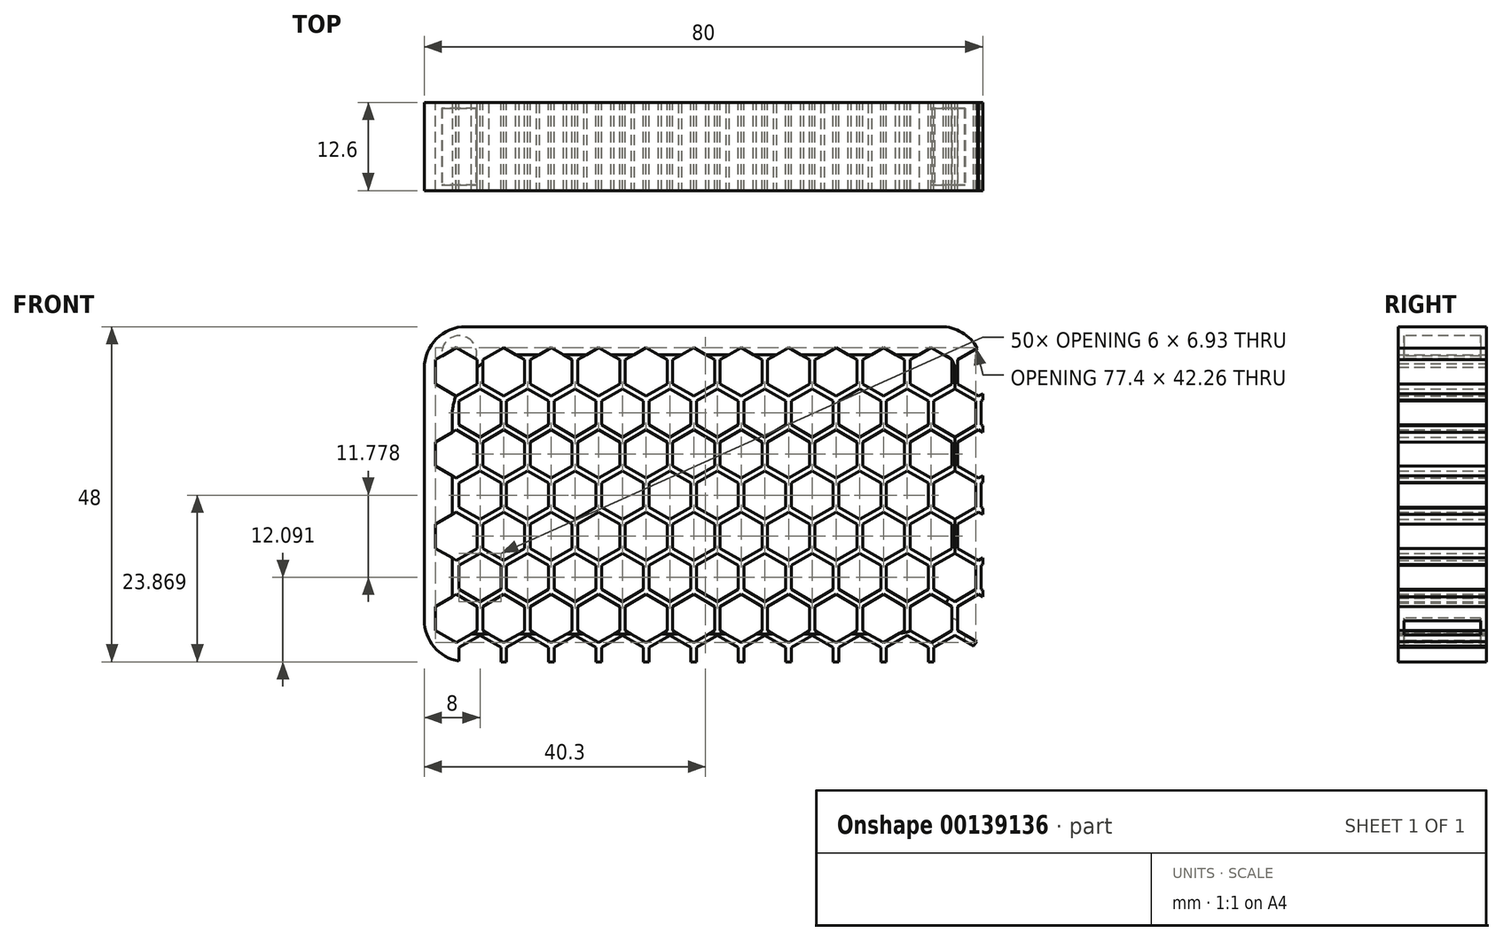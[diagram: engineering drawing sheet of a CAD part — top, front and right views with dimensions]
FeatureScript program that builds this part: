
annotation { "Feature Type Name" : "Feature", "Feature Type Description" : "" }
export const myFeature = defineFeature(function(context is Context, id is Id, definition is map)
    precondition{}
    {
        {
            var Q0;
            Q0=qCreatedBy(makeId("Front.planeOp"),FACE);
            var sketch = newSketch(context, id + "F0", { "sketchPlane" : qUnion([Q0])});
            skLineSegment(sketch, "E0.bottom", {"start": v(-34, 24) * mm, "end": v(34, 24) * mm});
            skLineSegment(sketch, "E0.top", {"start": v(-34, -24) * mm, "end": v(34, -24) * mm});
            skLineSegment(sketch, "E0.left", {"start": v(-40, 18) * mm, "end": v(-40, -18) * mm});
            skLineSegment(sketch, "E0.right", {"start": v(40, 18) * mm, "end": v(40, -18) * mm});
            skPoint(sketch, "E1", {"position": v(0, 24) * mm});
            skPoint(sketch, "E2", {"position": v(-40, 0) * mm});
            skPoint(sketch, "E3.visualSharp", {"position": v(-40, 24) * mm});
            skArc(sketch, "E3.filletArc", {"start": v(-34, 24) * mm, "mid": v(-38.24, 22.24) * mm, "end": v(-40, 18) * mm});
            skPoint(sketch, "E4.visualSharp", {"position": v(40, 24) * mm});
            skArc(sketch, "E4.filletArc", {"start": v(40, 18) * mm, "mid": v(38.24, 22.24) * mm, "end": v(34, 24) * mm});
            skPoint(sketch, "E5.visualSharp", {"position": v(40, -24) * mm});
            skArc(sketch, "E5.filletArc", {"start": v(34, -24) * mm, "mid": v(38.24, -22.24) * mm, "end": v(40, -18) * mm});
            skPoint(sketch, "E6.visualSharp", {"position": v(-40, -24) * mm});
            skArc(sketch, "E6.filletArc", {"start": v(-40, -18) * mm, "mid": v(-38.24, -22.24) * mm, "end": v(-34, -24) * mm});
            skLineSegment(sketch, "E7.0", {"start": v(-27, 20) * mm, "end": v(34, 20) * mm});
            skLineSegment(sketch, "E7.1", {"start": v(-36, 11) * mm, "end": v(-36, -18) * mm});
            skLineSegment(sketch, "E7.2", {"start": v(-34, -20) * mm, "end": v(27, -20) * mm});
            skLineSegment(sketch, "E7.3", {"start": v(36, 18) * mm, "end": v(36, -11) * mm});
            skPoint(sketch, "E8.visualSharp", {"position": v(36, 20) * mm});
            skArc(sketch, "E8.filletArc", {"start": v(36, 18) * mm, "mid": v(35.41, 19.41) * mm, "end": v(34, 20) * mm});
            skPoint(sketch, "E9.visualSharp", {"position": v(36, -20) * mm});
            skPoint(sketch, "E10.visualSharp", {"position": v(-36, -20) * mm});
            skArc(sketch, "E10.filletArc", {"start": v(-36, -18) * mm, "mid": v(-35.41, -19.41) * mm, "end": v(-34, -20) * mm});
            skPoint(sketch, "E11.visualSharp", {"position": v(-36, 20) * mm});
            skArc(sketch, "E12.filletArc", {"start": v(-27, 20) * mm, "mid": v(-33.36, 17.36) * mm, "end": v(-36, 11) * mm});
            skArc(sketch, "E13.filletArc", {"start": v(27, -20) * mm, "mid": v(33.36, -17.36) * mm, "end": v(36, -11) * mm});
            skSolve(sketch);
        }
        {
            var Q0;
            Q0=makeQuery(id+"F0.imprint","IMPRINT",FACE,{"disambiguationData":[TD([[makeQuery(id+"F0.imprint","IMPRINT",EDGE,{"derivedFrom":sQuery(id+"F0.wireOp",EDGE,"E0.bottom")}),-1.0]])]});
            var Q1;
            {var subQ0=sQuery(id+"F0.wireOp",EDGE,"E11.filletArc");Q1=makeQuery(id+"F0.imprint","IMPRINT",FACE,{"disambiguationData":[TD([[makeQuery(id+"F0.imprint","IMPRINT",EDGE,{"derivedFrom":subQ0}),1.0]])]});}
            var Q2;
            {var subQ0=sQuery(id+"F0.wireOp",EDGE,"E11.filletArc");Q2=makeQuery(id+"F0.imprint","IMPRINT",FACE,{"disambiguationData":[TD([[makeQuery(id+"F0.imprint","IMPRINT",EDGE,{"derivedFrom":subQ0}),-1.0]])]});}
            extrude(context, id + "F1", {"entities" : qUnion([Q0, Q1, Q2]), "endBound" : BoundingType.SYMMETRIC, "depth" : 12.6 * mm});
        }
        {
            var Q0;
            Q0=makeQuery(id+"F1.opExtrude","CAP_FACE",FACE,{"disambiguationData":[OSD([sQuery(id+"F0.wireOp",EDGE,"E0.bottom"),sQuery(id+"F0.wireOp",EDGE,"E0.top"),sQuery(id+"F0.wireOp",EDGE,"E0.left"),sQuery(id+"F0.wireOp",EDGE,"E0.right"),sQuery(id+"F0.wireOp",EDGE,"E3.filletArc"),sQuery(id+"F0.wireOp",EDGE,"E4.filletArc"),sQuery(id+"F0.wireOp",EDGE,"E5.filletArc"),sQuery(id+"F0.wireOp",EDGE,"E6.filletArc"),sQuery(id+"F0.wireOp",EDGE,"E7.0"),sQuery(id+"F0.wireOp",EDGE,"E7.1"),sQuery(id+"F0.wireOp",EDGE,"E7.2"),sQuery(id+"F0.wireOp",EDGE,"E7.3"),sQuery(id+"F0.wireOp",EDGE,"E8.filletArc"),sQuery(id+"F0.wireOp",EDGE,"E9.filletArc"),sQuery(id+"F0.wireOp",EDGE,"E10.filletArc"),sQuery(id+"F0.wireOp",EDGE,"E11.filletArc")])],"isStart":false});
            cPlane(context, id + "F2", {"entities" : qUnion([Q0]), "cplaneType" : CPlaneType.OFFSET, "offset" : 0.8 * mm, "oppositeDirection" : true, "width" : 150 * mm, "height" : 150 * mm});
        }
        {
            var Q0;
            Q0=qCreatedBy(id+"F2.planeOp",FACE);
            var sketch = newSketch(context, id + "F3", { "sketchPlane" : qUnion([Q0])});
            skPoint(sketch, "E14", {"position": v(-34.99, 20.2) * mm});
            skLineSegment(sketch, "E15", {"start": v(-34.99, 20.2) * mm, "end": v(34.99, -20.2) * mm, "construction": true});
            skCircle(sketch, "E16", {"center": v(-34.99, 20.2) * mm, "radius": 2.5 * mm});
            skCircle(sketch, "E17", {"center": v(34.99, -20.2) * mm, "radius": 2.5 * mm});
            skSolve(sketch);
        }
        {
            var Q0;
            Q0=makeQuery(id+"F0.imprint","IMPRINT",FACE,{"disambiguationData":[TD([[makeQuery(id+"F0.imprint","IMPRINT",EDGE,{"derivedFrom":sQuery(id+"F0.wireOp",EDGE,"E7.0")}),-1.0]])]});
            extrude(context, id + "F4", {"entities" : qUnion([Q0]), "endBound" : BoundingType.SYMMETRIC, "depth" : 12.6 * mm});
        }
        {
            var Q0;
            Q0=qCreatedBy(makeId("Front.planeOp"),FACE);
            var sketch = newSketch(context, id + "F5", { "sketchPlane" : qUnion([Q0])});
            skLineSegment(sketch, "E18.bottom", {"start": v(-38, 24) * mm, "end": v(38, 24) * mm, "construction": true});
            skLineSegment(sketch, "E18.top", {"start": v(-38, -24) * mm, "end": v(38, -24) * mm, "construction": true});
            skLineSegment(sketch, "E18.left", {"start": v(-38, 24) * mm, "end": v(-38, -24) * mm, "construction": true});
            skLineSegment(sketch, "E18.right", {"start": v(38, 24) * mm, "end": v(38, -24) * mm, "construction": true});
            skCircle(sketch, "E19.cCircle", {"center": v(-35.4, 17.54) * mm, "radius": 3 * mm, "construction": true});
            skLineSegment(sketch, "E19.0", {"start": v(-32.4, 19.27) * mm, "end": v(-32.4, 15.8) * mm});
            skLineSegment(sketch, "E19.1", {"start": v(-32.4, 15.8) * mm, "end": v(-35.4, 14.07) * mm});
            skLineSegment(sketch, "E19.2", {"start": v(-35.4, 14.07) * mm, "end": v(-38.4, 15.8) * mm});
            skLineSegment(sketch, "E19.3", {"start": v(-38.4, 15.8) * mm, "end": v(-38.4, 19.27) * mm});
            skLineSegment(sketch, "E19.4", {"start": v(-38.4, 19.27) * mm, "end": v(-35.4, 21) * mm});
            skLineSegment(sketch, "E19.5", {"start": v(-35.4, 21) * mm, "end": v(-32.4, 19.27) * mm});
            skPoint(sketch, "E19.0.midPoint", {"position": v(-32.4, 17.54) * mm});
            skPoint(sketch, "E20", {"position": v(0, -24) * mm});
            skPoint(sketch, "E21", {"position": v(38, 0) * mm});
            skCircle(sketch, "E22.cCircle", {"center": v(-32, 11.65) * mm, "radius": 3 * mm, "construction": true});
            skLineSegment(sketch, "E22.0", {"start": v(-29, 13.38) * mm, "end": v(-29, 9.91) * mm});
            skLineSegment(sketch, "E22.1", {"start": v(-29, 9.91) * mm, "end": v(-32, 8.18) * mm});
            skLineSegment(sketch, "E22.2", {"start": v(-32, 8.18) * mm, "end": v(-35, 9.91) * mm});
            skLineSegment(sketch, "E22.3", {"start": v(-35, 9.91) * mm, "end": v(-35, 13.38) * mm});
            skLineSegment(sketch, "E22.4", {"start": v(-35, 13.38) * mm, "end": v(-32, 15.11) * mm});
            skLineSegment(sketch, "E22.5", {"start": v(-32, 15.11) * mm, "end": v(-29, 13.38) * mm});
            skPoint(sketch, "E22.0.midPoint", {"position": v(-29, 11.65) * mm});
            skLineSegment(sketch, "E23.1.0.0", {"start": v(-28.6, 14.07) * mm, "end": v(-31.6, 15.8) * mm});
            skLineSegment(sketch, "E23.1.0.1", {"start": v(-31.6, 15.8) * mm, "end": v(-31.6, 19.27) * mm});
            skLineSegment(sketch, "E23.1.0.2", {"start": v(-31.6, 19.27) * mm, "end": v(-28.6, 21) * mm});
            skLineSegment(sketch, "E23.1.0.3", {"start": v(-28.6, 21) * mm, "end": v(-25.6, 19.27) * mm});
            skLineSegment(sketch, "E23.1.0.4", {"start": v(-25.6, 19.27) * mm, "end": v(-25.6, 15.8) * mm});
            skLineSegment(sketch, "E23.1.0.5", {"start": v(-25.6, 15.8) * mm, "end": v(-28.6, 14.07) * mm});
            skLineSegment(sketch, "E23.1.0.6", {"start": v(-25.2, 8.18) * mm, "end": v(-28.2, 9.91) * mm});
            skLineSegment(sketch, "E23.1.0.7", {"start": v(-28.2, 9.91) * mm, "end": v(-28.2, 13.38) * mm});
            skLineSegment(sketch, "E23.1.0.8", {"start": v(-25.2, 15.11) * mm, "end": v(-22.2, 13.38) * mm});
            skLineSegment(sketch, "E23.1.0.9", {"start": v(-22.2, 13.38) * mm, "end": v(-22.2, 9.91) * mm});
            skLineSegment(sketch, "E23.1.0.10", {"start": v(-22.2, 9.91) * mm, "end": v(-25.2, 8.18) * mm});
            skLineSegment(sketch, "E23.1.0.11", {"start": v(-28.2, 13.38) * mm, "end": v(-25.2, 15.11) * mm});
            skLineSegment(sketch, "E23.2.0.0", {"start": v(-21.8, 14.07) * mm, "end": v(-24.8, 15.8) * mm});
            skLineSegment(sketch, "E23.2.0.1", {"start": v(-24.8, 15.8) * mm, "end": v(-24.8, 19.27) * mm});
            skLineSegment(sketch, "E23.2.0.2", {"start": v(-24.8, 19.27) * mm, "end": v(-21.8, 21) * mm});
            skLineSegment(sketch, "E23.2.0.3", {"start": v(-21.8, 21) * mm, "end": v(-18.8, 19.27) * mm});
            skLineSegment(sketch, "E23.2.0.4", {"start": v(-18.8, 19.27) * mm, "end": v(-18.8, 15.8) * mm});
            skLineSegment(sketch, "E23.2.0.5", {"start": v(-18.8, 15.8) * mm, "end": v(-21.8, 14.07) * mm});
            skLineSegment(sketch, "E23.2.0.6", {"start": v(-18.4, 8.18) * mm, "end": v(-21.4, 9.91) * mm});
            skLineSegment(sketch, "E23.2.0.7", {"start": v(-21.4, 9.91) * mm, "end": v(-21.4, 13.38) * mm});
            skLineSegment(sketch, "E23.2.0.8", {"start": v(-18.4, 15.11) * mm, "end": v(-15.4, 13.38) * mm});
            skLineSegment(sketch, "E23.2.0.9", {"start": v(-15.4, 13.38) * mm, "end": v(-15.4, 9.91) * mm});
            skLineSegment(sketch, "E23.2.0.10", {"start": v(-15.4, 9.91) * mm, "end": v(-18.4, 8.18) * mm});
            skLineSegment(sketch, "E23.2.0.11", {"start": v(-21.4, 13.38) * mm, "end": v(-18.4, 15.11) * mm});
            skLineSegment(sketch, "E23.3.0.0", {"start": v(-15, 14.07) * mm, "end": v(-18, 15.8) * mm});
            skLineSegment(sketch, "E23.3.0.1", {"start": v(-18, 15.8) * mm, "end": v(-18, 19.27) * mm});
            skLineSegment(sketch, "E23.3.0.2", {"start": v(-18, 19.27) * mm, "end": v(-15, 21) * mm});
            skLineSegment(sketch, "E23.3.0.3", {"start": v(-15, 21) * mm, "end": v(-12, 19.27) * mm});
            skLineSegment(sketch, "E23.3.0.4", {"start": v(-12, 19.27) * mm, "end": v(-12, 15.8) * mm});
            skLineSegment(sketch, "E23.3.0.5", {"start": v(-12, 15.8) * mm, "end": v(-15, 14.07) * mm});
            skLineSegment(sketch, "E23.3.0.6", {"start": v(-11.6, 8.18) * mm, "end": v(-14.6, 9.91) * mm});
            skLineSegment(sketch, "E23.3.0.7", {"start": v(-14.6, 9.91) * mm, "end": v(-14.6, 13.38) * mm});
            skLineSegment(sketch, "E23.3.0.8", {"start": v(-11.6, 15.11) * mm, "end": v(-8.6, 13.38) * mm});
            skLineSegment(sketch, "E23.3.0.9", {"start": v(-8.6, 13.38) * mm, "end": v(-8.6, 9.91) * mm});
            skLineSegment(sketch, "E23.3.0.10", {"start": v(-8.6, 9.91) * mm, "end": v(-11.6, 8.18) * mm});
            skLineSegment(sketch, "E23.3.0.11", {"start": v(-14.6, 13.38) * mm, "end": v(-11.6, 15.11) * mm});
            skLineSegment(sketch, "E23.4.0.0", {"start": v(-8.2, 14.07) * mm, "end": v(-11.2, 15.8) * mm});
            skLineSegment(sketch, "E23.4.0.1", {"start": v(-11.2, 15.8) * mm, "end": v(-11.2, 19.27) * mm});
            skLineSegment(sketch, "E23.4.0.2", {"start": v(-11.2, 19.27) * mm, "end": v(-8.2, 21) * mm});
            skLineSegment(sketch, "E23.4.0.3", {"start": v(-8.2, 21) * mm, "end": v(-5.2, 19.27) * mm});
            skLineSegment(sketch, "E23.4.0.4", {"start": v(-5.2, 19.27) * mm, "end": v(-5.2, 15.8) * mm});
            skLineSegment(sketch, "E23.4.0.5", {"start": v(-5.2, 15.8) * mm, "end": v(-8.2, 14.07) * mm});
            skLineSegment(sketch, "E23.4.0.6", {"start": v(-4.8, 8.18) * mm, "end": v(-7.8, 9.91) * mm});
            skLineSegment(sketch, "E23.4.0.7", {"start": v(-7.8, 9.91) * mm, "end": v(-7.8, 13.38) * mm});
            skLineSegment(sketch, "E23.4.0.8", {"start": v(-4.8, 15.11) * mm, "end": v(-1.8, 13.38) * mm});
            skLineSegment(sketch, "E23.4.0.9", {"start": v(-1.8, 13.38) * mm, "end": v(-1.8, 9.91) * mm});
            skLineSegment(sketch, "E23.4.0.10", {"start": v(-1.8, 9.91) * mm, "end": v(-4.8, 8.18) * mm});
            skLineSegment(sketch, "E23.4.0.11", {"start": v(-7.8, 13.38) * mm, "end": v(-4.8, 15.11) * mm});
            skLineSegment(sketch, "E23.5.0.0", {"start": v(-1.4, 14.07) * mm, "end": v(-4.4, 15.8) * mm});
            skLineSegment(sketch, "E23.5.0.1", {"start": v(-4.4, 15.8) * mm, "end": v(-4.4, 19.27) * mm});
            skLineSegment(sketch, "E23.5.0.2", {"start": v(-4.4, 19.27) * mm, "end": v(-1.4, 21) * mm});
            skLineSegment(sketch, "E23.5.0.3", {"start": v(-1.4, 21) * mm, "end": v(1.6, 19.27) * mm});
            skLineSegment(sketch, "E23.5.0.4", {"start": v(1.6, 19.27) * mm, "end": v(1.6, 15.8) * mm});
            skLineSegment(sketch, "E23.5.0.5", {"start": v(1.6, 15.8) * mm, "end": v(-1.4, 14.07) * mm});
            skLineSegment(sketch, "E23.5.0.6", {"start": v(2, 8.18) * mm, "end": v(-1, 9.91) * mm});
            skLineSegment(sketch, "E23.5.0.7", {"start": v(-1, 9.91) * mm, "end": v(-1, 13.38) * mm});
            skLineSegment(sketch, "E23.5.0.8", {"start": v(2, 15.11) * mm, "end": v(5, 13.38) * mm});
            skLineSegment(sketch, "E23.5.0.9", {"start": v(5, 13.38) * mm, "end": v(5, 9.91) * mm});
            skLineSegment(sketch, "E23.5.0.10", {"start": v(5, 9.91) * mm, "end": v(2, 8.18) * mm});
            skLineSegment(sketch, "E23.5.0.11", {"start": v(-1, 13.38) * mm, "end": v(2, 15.11) * mm});
            skLineSegment(sketch, "E23.6.0.0", {"start": v(5.4, 14.07) * mm, "end": v(2.4, 15.8) * mm});
            skLineSegment(sketch, "E23.6.0.1", {"start": v(2.4, 15.8) * mm, "end": v(2.4, 19.27) * mm});
            skLineSegment(sketch, "E23.6.0.2", {"start": v(2.4, 19.27) * mm, "end": v(5.4, 21) * mm});
            skLineSegment(sketch, "E23.6.0.3", {"start": v(5.4, 21) * mm, "end": v(8.4, 19.27) * mm});
            skLineSegment(sketch, "E23.6.0.4", {"start": v(8.4, 19.27) * mm, "end": v(8.4, 15.8) * mm});
            skLineSegment(sketch, "E23.6.0.5", {"start": v(8.4, 15.8) * mm, "end": v(5.4, 14.07) * mm});
            skLineSegment(sketch, "E23.6.0.6", {"start": v(8.8, 8.18) * mm, "end": v(5.8, 9.91) * mm});
            skLineSegment(sketch, "E23.6.0.7", {"start": v(5.8, 9.91) * mm, "end": v(5.8, 13.38) * mm});
            skLineSegment(sketch, "E23.6.0.8", {"start": v(8.8, 15.11) * mm, "end": v(11.8, 13.38) * mm});
            skLineSegment(sketch, "E23.6.0.9", {"start": v(11.8, 13.38) * mm, "end": v(11.8, 9.91) * mm});
            skLineSegment(sketch, "E23.6.0.10", {"start": v(11.8, 9.91) * mm, "end": v(8.8, 8.18) * mm});
            skLineSegment(sketch, "E23.6.0.11", {"start": v(5.8, 13.38) * mm, "end": v(8.8, 15.11) * mm});
            skLineSegment(sketch, "E23.7.0.0", {"start": v(12.2, 14.07) * mm, "end": v(9.2, 15.8) * mm});
            skLineSegment(sketch, "E23.7.0.1", {"start": v(9.2, 15.8) * mm, "end": v(9.2, 19.27) * mm});
            skLineSegment(sketch, "E23.7.0.2", {"start": v(9.2, 19.27) * mm, "end": v(12.2, 21) * mm});
            skLineSegment(sketch, "E23.7.0.3", {"start": v(12.2, 21) * mm, "end": v(15.2, 19.27) * mm});
            skLineSegment(sketch, "E23.7.0.4", {"start": v(15.2, 19.27) * mm, "end": v(15.2, 15.8) * mm});
            skLineSegment(sketch, "E23.7.0.5", {"start": v(15.2, 15.8) * mm, "end": v(12.2, 14.07) * mm});
            skLineSegment(sketch, "E23.7.0.6", {"start": v(15.6, 8.18) * mm, "end": v(12.6, 9.91) * mm});
            skLineSegment(sketch, "E23.7.0.7", {"start": v(12.6, 9.91) * mm, "end": v(12.6, 13.38) * mm});
            skLineSegment(sketch, "E23.7.0.8", {"start": v(15.6, 15.11) * mm, "end": v(18.6, 13.38) * mm});
            skLineSegment(sketch, "E23.7.0.9", {"start": v(18.6, 13.38) * mm, "end": v(18.6, 9.91) * mm});
            skLineSegment(sketch, "E23.7.0.10", {"start": v(18.6, 9.91) * mm, "end": v(15.6, 8.18) * mm});
            skLineSegment(sketch, "E23.7.0.11", {"start": v(12.6, 13.38) * mm, "end": v(15.6, 15.11) * mm});
            skLineSegment(sketch, "E23.8.0.0", {"start": v(19, 14.07) * mm, "end": v(16, 15.8) * mm});
            skLineSegment(sketch, "E23.8.0.1", {"start": v(16, 15.8) * mm, "end": v(16, 19.27) * mm});
            skLineSegment(sketch, "E23.8.0.2", {"start": v(16, 19.27) * mm, "end": v(19, 21) * mm});
            skLineSegment(sketch, "E23.8.0.3", {"start": v(19, 21) * mm, "end": v(22, 19.27) * mm});
            skLineSegment(sketch, "E23.8.0.4", {"start": v(22, 19.27) * mm, "end": v(22, 15.8) * mm});
            skLineSegment(sketch, "E23.8.0.5", {"start": v(22, 15.8) * mm, "end": v(19, 14.07) * mm});
            skLineSegment(sketch, "E23.8.0.6", {"start": v(22.4, 8.18) * mm, "end": v(19.4, 9.91) * mm});
            skLineSegment(sketch, "E23.8.0.7", {"start": v(19.4, 9.91) * mm, "end": v(19.4, 13.38) * mm});
            skLineSegment(sketch, "E23.8.0.8", {"start": v(22.4, 15.11) * mm, "end": v(25.4, 13.38) * mm});
            skLineSegment(sketch, "E23.8.0.9", {"start": v(25.4, 13.38) * mm, "end": v(25.4, 9.91) * mm});
            skLineSegment(sketch, "E23.8.0.10", {"start": v(25.4, 9.91) * mm, "end": v(22.4, 8.18) * mm});
            skLineSegment(sketch, "E23.8.0.11", {"start": v(19.4, 13.38) * mm, "end": v(22.4, 15.11) * mm});
            skLineSegment(sketch, "E23.9.0.0", {"start": v(25.8, 14.07) * mm, "end": v(22.8, 15.8) * mm});
            skLineSegment(sketch, "E23.9.0.1", {"start": v(22.8, 15.8) * mm, "end": v(22.8, 19.27) * mm});
            skLineSegment(sketch, "E23.9.0.2", {"start": v(22.8, 19.27) * mm, "end": v(25.8, 21) * mm});
            skLineSegment(sketch, "E23.9.0.3", {"start": v(25.8, 21) * mm, "end": v(28.8, 19.27) * mm});
            skLineSegment(sketch, "E23.9.0.4", {"start": v(28.8, 19.27) * mm, "end": v(28.8, 15.8) * mm});
            skLineSegment(sketch, "E23.9.0.5", {"start": v(28.8, 15.8) * mm, "end": v(25.8, 14.07) * mm});
            skLineSegment(sketch, "E23.9.0.6", {"start": v(29.2, 8.18) * mm, "end": v(26.2, 9.91) * mm});
            skLineSegment(sketch, "E23.9.0.7", {"start": v(26.2, 9.91) * mm, "end": v(26.2, 13.38) * mm});
            skLineSegment(sketch, "E23.9.0.8", {"start": v(29.2, 15.11) * mm, "end": v(32.2, 13.38) * mm});
            skLineSegment(sketch, "E23.9.0.9", {"start": v(32.2, 13.38) * mm, "end": v(32.2, 9.91) * mm});
            skLineSegment(sketch, "E23.9.0.10", {"start": v(32.2, 9.91) * mm, "end": v(29.2, 8.18) * mm});
            skLineSegment(sketch, "E23.9.0.11", {"start": v(26.2, 13.38) * mm, "end": v(29.2, 15.11) * mm});
            skLineSegment(sketch, "E23.10.0.0", {"start": v(32.6, 14.07) * mm, "end": v(29.6, 15.8) * mm});
            skLineSegment(sketch, "E23.10.0.1", {"start": v(29.6, 15.8) * mm, "end": v(29.6, 19.27) * mm});
            skLineSegment(sketch, "E23.10.0.2", {"start": v(29.6, 19.27) * mm, "end": v(32.6, 21) * mm});
            skLineSegment(sketch, "E23.10.0.3", {"start": v(32.6, 21) * mm, "end": v(35.6, 19.27) * mm});
            skLineSegment(sketch, "E23.10.0.4", {"start": v(35.6, 19.27) * mm, "end": v(35.6, 15.8) * mm});
            skLineSegment(sketch, "E23.10.0.5", {"start": v(35.6, 15.8) * mm, "end": v(32.6, 14.07) * mm});
            skLineSegment(sketch, "E23.10.0.6", {"start": v(36, 8.18) * mm, "end": v(33, 9.91) * mm});
            skLineSegment(sketch, "E23.10.0.7", {"start": v(33, 9.91) * mm, "end": v(33, 13.38) * mm});
            skLineSegment(sketch, "E23.10.0.8", {"start": v(36, 15.11) * mm, "end": v(39, 13.38) * mm});
            skLineSegment(sketch, "E23.10.0.9", {"start": v(39, 13.38) * mm, "end": v(39, 9.91) * mm});
            skLineSegment(sketch, "E23.10.0.10", {"start": v(39, 9.91) * mm, "end": v(36, 8.18) * mm});
            skLineSegment(sketch, "E23.10.0.11", {"start": v(33, 13.38) * mm, "end": v(36, 15.11) * mm});
            skLineSegment(sketch, "E23.11.0.0", {"start": v(39.4, 14.07) * mm, "end": v(36.4, 15.8) * mm});
            skLineSegment(sketch, "E23.11.0.1", {"start": v(36.4, 15.8) * mm, "end": v(36.4, 19.27) * mm});
            skLineSegment(sketch, "E23.11.0.2", {"start": v(36.4, 19.27) * mm, "end": v(39.4, 21) * mm});
            skLineSegment(sketch, "E23.11.0.3", {"start": v(39.4, 21) * mm, "end": v(42.4, 19.27) * mm});
            skLineSegment(sketch, "E23.11.0.4", {"start": v(42.4, 19.27) * mm, "end": v(42.4, 15.8) * mm});
            skLineSegment(sketch, "E23.11.0.5", {"start": v(42.4, 15.8) * mm, "end": v(39.4, 14.07) * mm});
            skLineSegment(sketch, "E23.11.0.6", {"start": v(42.8, 8.18) * mm, "end": v(39.8, 9.91) * mm});
            skLineSegment(sketch, "E23.11.0.7", {"start": v(39.8, 9.91) * mm, "end": v(39.8, 13.38) * mm});
            skLineSegment(sketch, "E23.11.0.8", {"start": v(42.8, 15.11) * mm, "end": v(45.8, 13.38) * mm});
            skLineSegment(sketch, "E23.11.0.9", {"start": v(45.8, 13.38) * mm, "end": v(45.8, 9.91) * mm});
            skLineSegment(sketch, "E23.11.0.10", {"start": v(45.8, 9.91) * mm, "end": v(42.8, 8.18) * mm});
            skLineSegment(sketch, "E23.11.0.11", {"start": v(39.8, 13.38) * mm, "end": v(42.8, 15.11) * mm});
            skLineSegment(sketch, "E23.direction1", {"start": v(-35, 9.91) * mm, "end": v(-28.2, 9.91) * mm, "construction": true});
            skLineSegment(sketch, "E23.direction2", {"start": v(-35, 9.91) * mm, "end": v(-35, -1.86) * mm, "construction": true});
            skLineSegment(sketch, "E24.0.0.1", {"start": v(-35.4, 2.3) * mm, "end": v(-38.4, 4.03) * mm});
            skLineSegment(sketch, "E24.3.0.1", {"start": v(-38.4, 4.03) * mm, "end": v(-38.4, 7.49) * mm});
            skLineSegment(sketch, "E24.6.0.1", {"start": v(-38.4, 7.49) * mm, "end": v(-35.4, 9.22) * mm});
            skLineSegment(sketch, "E24.9.0.1", {"start": v(-35.4, 9.22) * mm, "end": v(-32.4, 7.49) * mm});
            skLineSegment(sketch, "E24.12.0.1", {"start": v(-32.4, 7.49) * mm, "end": v(-32.4, 4.03) * mm});
            skLineSegment(sketch, "E24.15.0.1", {"start": v(-32.4, 4.03) * mm, "end": v(-35.4, 2.3) * mm});
            skLineSegment(sketch, "E24.18.0.1", {"start": v(-32, -3.6) * mm, "end": v(-35, -1.86) * mm});
            skLineSegment(sketch, "E24.21.0.1", {"start": v(-35, -1.86) * mm, "end": v(-35, 1.6) * mm});
            skLineSegment(sketch, "E24.24.0.1", {"start": v(-32, 3.33) * mm, "end": v(-29, 1.6) * mm});
            skLineSegment(sketch, "E24.27.0.1", {"start": v(-29, 1.6) * mm, "end": v(-29, -1.86) * mm});
            skLineSegment(sketch, "E24.30.0.1", {"start": v(-29, -1.86) * mm, "end": v(-32, -3.6) * mm});
            skLineSegment(sketch, "E24.33.0.1", {"start": v(-35, 1.6) * mm, "end": v(-32, 3.33) * mm});
            skLineSegment(sketch, "E24.0.1.1", {"start": v(-28.6, 2.3) * mm, "end": v(-31.6, 4.03) * mm});
            skLineSegment(sketch, "E24.3.1.1", {"start": v(-31.6, 4.03) * mm, "end": v(-31.6, 7.49) * mm});
            skLineSegment(sketch, "E24.6.1.1", {"start": v(-31.6, 7.49) * mm, "end": v(-28.6, 9.22) * mm});
            skLineSegment(sketch, "E24.9.1.1", {"start": v(-28.6, 9.22) * mm, "end": v(-25.6, 7.49) * mm});
            skLineSegment(sketch, "E24.12.1.1", {"start": v(-25.6, 7.49) * mm, "end": v(-25.6, 4.03) * mm});
            skLineSegment(sketch, "E24.15.1.1", {"start": v(-25.6, 4.03) * mm, "end": v(-28.6, 2.3) * mm});
            skLineSegment(sketch, "E24.18.1.1", {"start": v(-25.2, -3.6) * mm, "end": v(-28.2, -1.86) * mm});
            skLineSegment(sketch, "E24.21.1.1", {"start": v(-28.2, -1.86) * mm, "end": v(-28.2, 1.6) * mm});
            skLineSegment(sketch, "E24.24.1.1", {"start": v(-25.2, 3.33) * mm, "end": v(-22.2, 1.6) * mm});
            skLineSegment(sketch, "E24.27.1.1", {"start": v(-22.2, 1.6) * mm, "end": v(-22.2, -1.86) * mm});
            skLineSegment(sketch, "E24.30.1.1", {"start": v(-22.2, -1.86) * mm, "end": v(-25.2, -3.6) * mm});
            skLineSegment(sketch, "E24.33.1.1", {"start": v(-28.2, 1.6) * mm, "end": v(-25.2, 3.33) * mm});
            skLineSegment(sketch, "E24.0.2.1", {"start": v(-21.8, 2.3) * mm, "end": v(-24.8, 4.03) * mm});
            skLineSegment(sketch, "E24.3.2.1", {"start": v(-24.8, 4.03) * mm, "end": v(-24.8, 7.49) * mm});
            skLineSegment(sketch, "E24.6.2.1", {"start": v(-24.8, 7.49) * mm, "end": v(-21.8, 9.22) * mm});
            skLineSegment(sketch, "E24.9.2.1", {"start": v(-21.8, 9.22) * mm, "end": v(-18.8, 7.49) * mm});
            skLineSegment(sketch, "E24.12.2.1", {"start": v(-18.8, 7.49) * mm, "end": v(-18.8, 4.03) * mm});
            skLineSegment(sketch, "E24.15.2.1", {"start": v(-18.8, 4.03) * mm, "end": v(-21.8, 2.3) * mm});
            skLineSegment(sketch, "E24.18.2.1", {"start": v(-18.4, -3.6) * mm, "end": v(-21.4, -1.86) * mm});
            skLineSegment(sketch, "E24.21.2.1", {"start": v(-21.4, -1.86) * mm, "end": v(-21.4, 1.6) * mm});
            skLineSegment(sketch, "E24.24.2.1", {"start": v(-18.4, 3.33) * mm, "end": v(-15.4, 1.6) * mm});
            skLineSegment(sketch, "E24.27.2.1", {"start": v(-15.4, 1.6) * mm, "end": v(-15.4, -1.86) * mm});
            skLineSegment(sketch, "E24.30.2.1", {"start": v(-15.4, -1.86) * mm, "end": v(-18.4, -3.6) * mm});
            skLineSegment(sketch, "E24.33.2.1", {"start": v(-21.4, 1.6) * mm, "end": v(-18.4, 3.33) * mm});
            skLineSegment(sketch, "E24.0.3.1", {"start": v(-15, 2.3) * mm, "end": v(-18, 4.03) * mm});
            skLineSegment(sketch, "E24.3.3.1", {"start": v(-18, 4.03) * mm, "end": v(-18, 7.49) * mm});
            skLineSegment(sketch, "E24.6.3.1", {"start": v(-18, 7.49) * mm, "end": v(-15, 9.22) * mm});
            skLineSegment(sketch, "E24.9.3.1", {"start": v(-15, 9.22) * mm, "end": v(-12, 7.49) * mm});
            skLineSegment(sketch, "E24.12.3.1", {"start": v(-12, 7.49) * mm, "end": v(-12, 4.03) * mm});
            skLineSegment(sketch, "E24.15.3.1", {"start": v(-12, 4.03) * mm, "end": v(-15, 2.3) * mm});
            skLineSegment(sketch, "E24.18.3.1", {"start": v(-11.6, -3.6) * mm, "end": v(-14.6, -1.86) * mm});
            skLineSegment(sketch, "E24.21.3.1", {"start": v(-14.6, -1.86) * mm, "end": v(-14.6, 1.6) * mm});
            skLineSegment(sketch, "E24.24.3.1", {"start": v(-11.6, 3.33) * mm, "end": v(-8.6, 1.6) * mm});
            skLineSegment(sketch, "E24.27.3.1", {"start": v(-8.6, 1.6) * mm, "end": v(-8.6, -1.86) * mm});
            skLineSegment(sketch, "E24.30.3.1", {"start": v(-8.6, -1.86) * mm, "end": v(-11.6, -3.6) * mm});
            skLineSegment(sketch, "E24.33.3.1", {"start": v(-14.6, 1.6) * mm, "end": v(-11.6, 3.33) * mm});
            skLineSegment(sketch, "E24.0.4.1", {"start": v(-8.2, 2.3) * mm, "end": v(-11.2, 4.03) * mm});
            skLineSegment(sketch, "E24.3.4.1", {"start": v(-11.2, 4.03) * mm, "end": v(-11.2, 7.49) * mm});
            skLineSegment(sketch, "E24.6.4.1", {"start": v(-11.2, 7.49) * mm, "end": v(-8.2, 9.22) * mm});
            skLineSegment(sketch, "E24.9.4.1", {"start": v(-8.2, 9.22) * mm, "end": v(-5.2, 7.49) * mm});
            skLineSegment(sketch, "E24.12.4.1", {"start": v(-5.2, 7.49) * mm, "end": v(-5.2, 4.03) * mm});
            skLineSegment(sketch, "E24.15.4.1", {"start": v(-5.2, 4.03) * mm, "end": v(-8.2, 2.3) * mm});
            skLineSegment(sketch, "E24.18.4.1", {"start": v(-4.8, -3.6) * mm, "end": v(-7.8, -1.86) * mm});
            skLineSegment(sketch, "E24.21.4.1", {"start": v(-7.8, -1.86) * mm, "end": v(-7.8, 1.6) * mm});
            skLineSegment(sketch, "E24.24.4.1", {"start": v(-4.8, 3.33) * mm, "end": v(-1.8, 1.6) * mm});
            skLineSegment(sketch, "E24.27.4.1", {"start": v(-1.8, 1.6) * mm, "end": v(-1.8, -1.86) * mm});
            skLineSegment(sketch, "E24.30.4.1", {"start": v(-1.8, -1.86) * mm, "end": v(-4.8, -3.6) * mm});
            skLineSegment(sketch, "E24.33.4.1", {"start": v(-7.8, 1.6) * mm, "end": v(-4.8, 3.33) * mm});
            skLineSegment(sketch, "E24.0.5.1", {"start": v(-1.4, 2.3) * mm, "end": v(-4.4, 4.03) * mm});
            skLineSegment(sketch, "E24.3.5.1", {"start": v(-4.4, 4.03) * mm, "end": v(-4.4, 7.49) * mm});
            skLineSegment(sketch, "E24.6.5.1", {"start": v(-4.4, 7.49) * mm, "end": v(-1.4, 9.22) * mm});
            skLineSegment(sketch, "E24.9.5.1", {"start": v(-1.4, 9.22) * mm, "end": v(1.6, 7.49) * mm});
            skLineSegment(sketch, "E24.12.5.1", {"start": v(1.6, 7.49) * mm, "end": v(1.6, 4.03) * mm});
            skLineSegment(sketch, "E24.15.5.1", {"start": v(1.6, 4.03) * mm, "end": v(-1.4, 2.3) * mm});
            skLineSegment(sketch, "E24.18.5.1", {"start": v(2, -3.6) * mm, "end": v(-1, -1.86) * mm});
            skLineSegment(sketch, "E24.21.5.1", {"start": v(-1, -1.86) * mm, "end": v(-1, 1.6) * mm});
            skLineSegment(sketch, "E24.24.5.1", {"start": v(2, 3.33) * mm, "end": v(5, 1.6) * mm});
            skLineSegment(sketch, "E24.27.5.1", {"start": v(5, 1.6) * mm, "end": v(5, -1.86) * mm});
            skLineSegment(sketch, "E24.30.5.1", {"start": v(5, -1.86) * mm, "end": v(2, -3.6) * mm});
            skLineSegment(sketch, "E24.33.5.1", {"start": v(-1, 1.6) * mm, "end": v(2, 3.33) * mm});
            skLineSegment(sketch, "E24.0.6.1", {"start": v(5.4, 2.3) * mm, "end": v(2.4, 4.03) * mm});
            skLineSegment(sketch, "E24.3.6.1", {"start": v(2.4, 4.03) * mm, "end": v(2.4, 7.49) * mm});
            skLineSegment(sketch, "E24.6.6.1", {"start": v(2.4, 7.49) * mm, "end": v(5.4, 9.22) * mm});
            skLineSegment(sketch, "E24.9.6.1", {"start": v(5.4, 9.22) * mm, "end": v(8.4, 7.49) * mm});
            skLineSegment(sketch, "E24.12.6.1", {"start": v(8.4, 7.49) * mm, "end": v(8.4, 4.03) * mm});
            skLineSegment(sketch, "E24.15.6.1", {"start": v(8.4, 4.03) * mm, "end": v(5.4, 2.3) * mm});
            skLineSegment(sketch, "E24.18.6.1", {"start": v(8.8, -3.6) * mm, "end": v(5.8, -1.86) * mm});
            skLineSegment(sketch, "E24.21.6.1", {"start": v(5.8, -1.86) * mm, "end": v(5.8, 1.6) * mm});
            skLineSegment(sketch, "E24.24.6.1", {"start": v(8.8, 3.33) * mm, "end": v(11.8, 1.6) * mm});
            skLineSegment(sketch, "E24.27.6.1", {"start": v(11.8, 1.6) * mm, "end": v(11.8, -1.86) * mm});
            skLineSegment(sketch, "E24.30.6.1", {"start": v(11.8, -1.86) * mm, "end": v(8.8, -3.6) * mm});
            skLineSegment(sketch, "E24.33.6.1", {"start": v(5.8, 1.6) * mm, "end": v(8.8, 3.33) * mm});
            skLineSegment(sketch, "E24.0.7.1", {"start": v(12.2, 2.3) * mm, "end": v(9.2, 4.03) * mm});
            skLineSegment(sketch, "E24.3.7.1", {"start": v(9.2, 4.03) * mm, "end": v(9.2, 7.49) * mm});
            skLineSegment(sketch, "E24.6.7.1", {"start": v(9.2, 7.49) * mm, "end": v(12.2, 9.22) * mm});
            skLineSegment(sketch, "E24.9.7.1", {"start": v(12.2, 9.22) * mm, "end": v(15.2, 7.49) * mm});
            skLineSegment(sketch, "E24.12.7.1", {"start": v(15.2, 7.49) * mm, "end": v(15.2, 4.03) * mm});
            skLineSegment(sketch, "E24.15.7.1", {"start": v(15.2, 4.03) * mm, "end": v(12.2, 2.3) * mm});
            skLineSegment(sketch, "E24.18.7.1", {"start": v(15.6, -3.6) * mm, "end": v(12.6, -1.86) * mm});
            skLineSegment(sketch, "E24.21.7.1", {"start": v(12.6, -1.86) * mm, "end": v(12.6, 1.6) * mm});
            skLineSegment(sketch, "E24.24.7.1", {"start": v(15.6, 3.33) * mm, "end": v(18.6, 1.6) * mm});
            skLineSegment(sketch, "E24.27.7.1", {"start": v(18.6, 1.6) * mm, "end": v(18.6, -1.86) * mm});
            skLineSegment(sketch, "E24.30.7.1", {"start": v(18.6, -1.86) * mm, "end": v(15.6, -3.6) * mm});
            skLineSegment(sketch, "E24.33.7.1", {"start": v(12.6, 1.6) * mm, "end": v(15.6, 3.33) * mm});
            skLineSegment(sketch, "E24.0.8.1", {"start": v(19, 2.3) * mm, "end": v(16, 4.03) * mm});
            skLineSegment(sketch, "E24.3.8.1", {"start": v(16, 4.03) * mm, "end": v(16, 7.49) * mm});
            skLineSegment(sketch, "E24.6.8.1", {"start": v(16, 7.49) * mm, "end": v(19, 9.22) * mm});
            skLineSegment(sketch, "E24.9.8.1", {"start": v(19, 9.22) * mm, "end": v(22, 7.49) * mm});
            skLineSegment(sketch, "E24.12.8.1", {"start": v(22, 7.49) * mm, "end": v(22, 4.03) * mm});
            skLineSegment(sketch, "E24.15.8.1", {"start": v(22, 4.03) * mm, "end": v(19, 2.3) * mm});
            skLineSegment(sketch, "E24.18.8.1", {"start": v(22.4, -3.6) * mm, "end": v(19.4, -1.86) * mm});
            skLineSegment(sketch, "E24.21.8.1", {"start": v(19.4, -1.86) * mm, "end": v(19.4, 1.6) * mm});
            skLineSegment(sketch, "E24.24.8.1", {"start": v(22.4, 3.33) * mm, "end": v(25.4, 1.6) * mm});
            skLineSegment(sketch, "E24.27.8.1", {"start": v(25.4, 1.6) * mm, "end": v(25.4, -1.86) * mm});
            skLineSegment(sketch, "E24.30.8.1", {"start": v(25.4, -1.86) * mm, "end": v(22.4, -3.6) * mm});
            skLineSegment(sketch, "E24.33.8.1", {"start": v(19.4, 1.6) * mm, "end": v(22.4, 3.33) * mm});
            skLineSegment(sketch, "E24.0.9.1", {"start": v(25.8, 2.3) * mm, "end": v(22.8, 4.03) * mm});
            skLineSegment(sketch, "E24.3.9.1", {"start": v(22.8, 4.03) * mm, "end": v(22.8, 7.49) * mm});
            skLineSegment(sketch, "E24.6.9.1", {"start": v(22.8, 7.49) * mm, "end": v(25.8, 9.22) * mm});
            skLineSegment(sketch, "E24.9.9.1", {"start": v(25.8, 9.22) * mm, "end": v(28.8, 7.49) * mm});
            skLineSegment(sketch, "E24.12.9.1", {"start": v(28.8, 7.49) * mm, "end": v(28.8, 4.03) * mm});
            skLineSegment(sketch, "E24.15.9.1", {"start": v(28.8, 4.03) * mm, "end": v(25.8, 2.3) * mm});
            skLineSegment(sketch, "E24.18.9.1", {"start": v(29.2, -3.6) * mm, "end": v(26.2, -1.86) * mm});
            skLineSegment(sketch, "E24.21.9.1", {"start": v(26.2, -1.86) * mm, "end": v(26.2, 1.6) * mm});
            skLineSegment(sketch, "E24.24.9.1", {"start": v(29.2, 3.33) * mm, "end": v(32.2, 1.6) * mm});
            skLineSegment(sketch, "E24.27.9.1", {"start": v(32.2, 1.6) * mm, "end": v(32.2, -1.86) * mm});
            skLineSegment(sketch, "E24.30.9.1", {"start": v(32.2, -1.86) * mm, "end": v(29.2, -3.6) * mm});
            skLineSegment(sketch, "E24.33.9.1", {"start": v(26.2, 1.6) * mm, "end": v(29.2, 3.33) * mm});
            skLineSegment(sketch, "E24.0.10.1", {"start": v(32.6, 2.3) * mm, "end": v(29.6, 4.03) * mm});
            skLineSegment(sketch, "E24.3.10.1", {"start": v(29.6, 4.03) * mm, "end": v(29.6, 7.49) * mm});
            skLineSegment(sketch, "E24.6.10.1", {"start": v(29.6, 7.49) * mm, "end": v(32.6, 9.22) * mm});
            skLineSegment(sketch, "E24.9.10.1", {"start": v(32.6, 9.22) * mm, "end": v(35.6, 7.49) * mm});
            skLineSegment(sketch, "E24.12.10.1", {"start": v(35.6, 7.49) * mm, "end": v(35.6, 4.03) * mm});
            skLineSegment(sketch, "E24.15.10.1", {"start": v(35.6, 4.03) * mm, "end": v(32.6, 2.3) * mm});
            skLineSegment(sketch, "E24.18.10.1", {"start": v(36, -3.6) * mm, "end": v(33, -1.86) * mm});
            skLineSegment(sketch, "E24.21.10.1", {"start": v(33, -1.86) * mm, "end": v(33, 1.6) * mm});
            skLineSegment(sketch, "E24.24.10.1", {"start": v(36, 3.33) * mm, "end": v(39, 1.6) * mm});
            skLineSegment(sketch, "E24.27.10.1", {"start": v(39, 1.6) * mm, "end": v(39, -1.86) * mm});
            skLineSegment(sketch, "E24.30.10.1", {"start": v(39, -1.86) * mm, "end": v(36, -3.6) * mm});
            skLineSegment(sketch, "E24.33.10.1", {"start": v(33, 1.6) * mm, "end": v(36, 3.33) * mm});
            skLineSegment(sketch, "E24.0.11.1", {"start": v(39.4, 2.3) * mm, "end": v(36.4, 4.03) * mm});
            skLineSegment(sketch, "E24.3.11.1", {"start": v(36.4, 4.03) * mm, "end": v(36.4, 7.49) * mm});
            skLineSegment(sketch, "E24.6.11.1", {"start": v(36.4, 7.49) * mm, "end": v(39.4, 9.22) * mm});
            skLineSegment(sketch, "E24.9.11.1", {"start": v(39.4, 9.22) * mm, "end": v(42.4, 7.49) * mm});
            skLineSegment(sketch, "E24.12.11.1", {"start": v(42.4, 7.49) * mm, "end": v(42.4, 4.03) * mm});
            skLineSegment(sketch, "E24.15.11.1", {"start": v(42.4, 4.03) * mm, "end": v(39.4, 2.3) * mm});
            skLineSegment(sketch, "E24.18.11.1", {"start": v(42.8, -3.6) * mm, "end": v(39.8, -1.86) * mm});
            skLineSegment(sketch, "E24.21.11.1", {"start": v(39.8, -1.86) * mm, "end": v(39.8, 1.6) * mm});
            skLineSegment(sketch, "E24.24.11.1", {"start": v(42.8, 3.33) * mm, "end": v(45.8, 1.6) * mm});
            skLineSegment(sketch, "E24.27.11.1", {"start": v(45.8, 1.6) * mm, "end": v(45.8, -1.86) * mm});
            skLineSegment(sketch, "E24.30.11.1", {"start": v(45.8, -1.86) * mm, "end": v(42.8, -3.6) * mm});
            skLineSegment(sketch, "E24.33.11.1", {"start": v(39.8, 1.6) * mm, "end": v(42.8, 3.33) * mm});
            skLineSegment(sketch, "E25.0.0.2", {"start": v(-35.4, -9.48) * mm, "end": v(-38.4, -7.75) * mm});
            skLineSegment(sketch, "E25.3.0.2", {"start": v(-38.4, -7.75) * mm, "end": v(-38.4, -4.29) * mm});
            skLineSegment(sketch, "E25.6.0.2", {"start": v(-38.4, -4.29) * mm, "end": v(-35.4, -2.56) * mm});
            skLineSegment(sketch, "E25.9.0.2", {"start": v(-35.4, -2.56) * mm, "end": v(-32.4, -4.29) * mm});
            skLineSegment(sketch, "E25.12.0.2", {"start": v(-32.4, -4.29) * mm, "end": v(-32.4, -7.75) * mm});
            skLineSegment(sketch, "E25.15.0.2", {"start": v(-32.4, -7.75) * mm, "end": v(-35.4, -9.48) * mm});
            skLineSegment(sketch, "E25.18.0.2", {"start": v(-32, -15.37) * mm, "end": v(-35, -13.64) * mm});
            skLineSegment(sketch, "E25.21.0.2", {"start": v(-35, -13.64) * mm, "end": v(-35, -10.18) * mm});
            skLineSegment(sketch, "E25.24.0.2", {"start": v(-32, -8.44) * mm, "end": v(-29, -10.18) * mm});
            skLineSegment(sketch, "E25.27.0.2", {"start": v(-29, -10.18) * mm, "end": v(-29, -13.64) * mm});
            skLineSegment(sketch, "E25.30.0.2", {"start": v(-29, -13.64) * mm, "end": v(-32, -15.37) * mm});
            skLineSegment(sketch, "E25.33.0.2", {"start": v(-35, -10.18) * mm, "end": v(-32, -8.44) * mm});
            skLineSegment(sketch, "E25.0.0.3", {"start": v(-35.4, -21.26) * mm, "end": v(-38.4, -19.53) * mm});
            skLineSegment(sketch, "E25.3.0.3", {"start": v(-38.4, -19.53) * mm, "end": v(-38.4, -16.07) * mm});
            skLineSegment(sketch, "E25.6.0.3", {"start": v(-38.4, -16.07) * mm, "end": v(-35.4, -14.33) * mm});
            skLineSegment(sketch, "E25.9.0.3", {"start": v(-35.4, -14.33) * mm, "end": v(-32.4, -16.07) * mm});
            skLineSegment(sketch, "E25.12.0.3", {"start": v(-32.4, -16.07) * mm, "end": v(-32.4, -19.53) * mm});
            skLineSegment(sketch, "E25.15.0.3", {"start": v(-32.4, -19.53) * mm, "end": v(-35.4, -21.26) * mm});
            skLineSegment(sketch, "E25.18.0.3", {"start": v(-32, -27.15) * mm, "end": v(-35, -25.42) * mm});
            skLineSegment(sketch, "E25.21.0.3", {"start": v(-35, -25.42) * mm, "end": v(-35, -21.96) * mm});
            skLineSegment(sketch, "E25.24.0.3", {"start": v(-32, -20.22) * mm, "end": v(-29, -21.96) * mm});
            skLineSegment(sketch, "E25.27.0.3", {"start": v(-29, -21.96) * mm, "end": v(-29, -25.42) * mm});
            skLineSegment(sketch, "E25.30.0.3", {"start": v(-29, -25.42) * mm, "end": v(-32, -27.15) * mm});
            skLineSegment(sketch, "E25.33.0.3", {"start": v(-35, -21.96) * mm, "end": v(-32, -20.22) * mm});
            skLineSegment(sketch, "E25.0.1.2", {"start": v(-28.6, -9.48) * mm, "end": v(-31.6, -7.75) * mm});
            skLineSegment(sketch, "E25.3.1.2", {"start": v(-31.6, -7.75) * mm, "end": v(-31.6, -4.29) * mm});
            skLineSegment(sketch, "E25.6.1.2", {"start": v(-31.6, -4.29) * mm, "end": v(-28.6, -2.56) * mm});
            skLineSegment(sketch, "E25.9.1.2", {"start": v(-28.6, -2.56) * mm, "end": v(-25.6, -4.29) * mm});
            skLineSegment(sketch, "E25.12.1.2", {"start": v(-25.6, -4.29) * mm, "end": v(-25.6, -7.75) * mm});
            skLineSegment(sketch, "E25.15.1.2", {"start": v(-25.6, -7.75) * mm, "end": v(-28.6, -9.48) * mm});
            skLineSegment(sketch, "E25.18.1.2", {"start": v(-25.2, -15.37) * mm, "end": v(-28.2, -13.64) * mm});
            skLineSegment(sketch, "E25.21.1.2", {"start": v(-28.2, -13.64) * mm, "end": v(-28.2, -10.18) * mm});
            skLineSegment(sketch, "E25.24.1.2", {"start": v(-25.2, -8.44) * mm, "end": v(-22.2, -10.18) * mm});
            skLineSegment(sketch, "E25.27.1.2", {"start": v(-22.2, -10.18) * mm, "end": v(-22.2, -13.64) * mm});
            skLineSegment(sketch, "E25.30.1.2", {"start": v(-22.2, -13.64) * mm, "end": v(-25.2, -15.37) * mm});
            skLineSegment(sketch, "E25.33.1.2", {"start": v(-28.2, -10.18) * mm, "end": v(-25.2, -8.44) * mm});
            skLineSegment(sketch, "E25.0.1.3", {"start": v(-28.6, -21.26) * mm, "end": v(-31.6, -19.53) * mm});
            skLineSegment(sketch, "E25.3.1.3", {"start": v(-31.6, -19.53) * mm, "end": v(-31.6, -16.07) * mm});
            skLineSegment(sketch, "E25.6.1.3", {"start": v(-31.6, -16.07) * mm, "end": v(-28.6, -14.33) * mm});
            skLineSegment(sketch, "E25.9.1.3", {"start": v(-28.6, -14.33) * mm, "end": v(-25.6, -16.07) * mm});
            skLineSegment(sketch, "E25.12.1.3", {"start": v(-25.6, -16.07) * mm, "end": v(-25.6, -19.53) * mm});
            skLineSegment(sketch, "E25.15.1.3", {"start": v(-25.6, -19.53) * mm, "end": v(-28.6, -21.26) * mm});
            skLineSegment(sketch, "E25.18.1.3", {"start": v(-25.2, -27.15) * mm, "end": v(-28.2, -25.42) * mm});
            skLineSegment(sketch, "E25.21.1.3", {"start": v(-28.2, -25.42) * mm, "end": v(-28.2, -21.96) * mm});
            skLineSegment(sketch, "E25.24.1.3", {"start": v(-25.2, -20.22) * mm, "end": v(-22.2, -21.96) * mm});
            skLineSegment(sketch, "E25.27.1.3", {"start": v(-22.2, -21.96) * mm, "end": v(-22.2, -25.42) * mm});
            skLineSegment(sketch, "E25.30.1.3", {"start": v(-22.2, -25.42) * mm, "end": v(-25.2, -27.15) * mm});
            skLineSegment(sketch, "E25.33.1.3", {"start": v(-28.2, -21.96) * mm, "end": v(-25.2, -20.22) * mm});
            skLineSegment(sketch, "E25.0.2.2", {"start": v(-21.8, -9.48) * mm, "end": v(-24.8, -7.75) * mm});
            skLineSegment(sketch, "E25.3.2.2", {"start": v(-24.8, -7.75) * mm, "end": v(-24.8, -4.29) * mm});
            skLineSegment(sketch, "E25.6.2.2", {"start": v(-24.8, -4.29) * mm, "end": v(-21.8, -2.56) * mm});
            skLineSegment(sketch, "E25.9.2.2", {"start": v(-21.8, -2.56) * mm, "end": v(-18.8, -4.29) * mm});
            skLineSegment(sketch, "E25.12.2.2", {"start": v(-18.8, -4.29) * mm, "end": v(-18.8, -7.75) * mm});
            skLineSegment(sketch, "E25.15.2.2", {"start": v(-18.8, -7.75) * mm, "end": v(-21.8, -9.48) * mm});
            skLineSegment(sketch, "E25.18.2.2", {"start": v(-18.4, -15.37) * mm, "end": v(-21.4, -13.64) * mm});
            skLineSegment(sketch, "E25.21.2.2", {"start": v(-21.4, -13.64) * mm, "end": v(-21.4, -10.18) * mm});
            skLineSegment(sketch, "E25.24.2.2", {"start": v(-18.4, -8.44) * mm, "end": v(-15.4, -10.18) * mm});
            skLineSegment(sketch, "E25.27.2.2", {"start": v(-15.4, -10.18) * mm, "end": v(-15.4, -13.64) * mm});
            skLineSegment(sketch, "E25.30.2.2", {"start": v(-15.4, -13.64) * mm, "end": v(-18.4, -15.37) * mm});
            skLineSegment(sketch, "E25.33.2.2", {"start": v(-21.4, -10.18) * mm, "end": v(-18.4, -8.44) * mm});
            skLineSegment(sketch, "E25.0.2.3", {"start": v(-21.8, -21.26) * mm, "end": v(-24.8, -19.53) * mm});
            skLineSegment(sketch, "E25.3.2.3", {"start": v(-24.8, -19.53) * mm, "end": v(-24.8, -16.07) * mm});
            skLineSegment(sketch, "E25.6.2.3", {"start": v(-24.8, -16.07) * mm, "end": v(-21.8, -14.33) * mm});
            skLineSegment(sketch, "E25.9.2.3", {"start": v(-21.8, -14.33) * mm, "end": v(-18.8, -16.07) * mm});
            skLineSegment(sketch, "E25.12.2.3", {"start": v(-18.8, -16.07) * mm, "end": v(-18.8, -19.53) * mm});
            skLineSegment(sketch, "E25.15.2.3", {"start": v(-18.8, -19.53) * mm, "end": v(-21.8, -21.26) * mm});
            skLineSegment(sketch, "E25.18.2.3", {"start": v(-18.4, -27.15) * mm, "end": v(-21.4, -25.42) * mm});
            skLineSegment(sketch, "E25.21.2.3", {"start": v(-21.4, -25.42) * mm, "end": v(-21.4, -21.96) * mm});
            skLineSegment(sketch, "E25.24.2.3", {"start": v(-18.4, -20.22) * mm, "end": v(-15.4, -21.96) * mm});
            skLineSegment(sketch, "E25.27.2.3", {"start": v(-15.4, -21.96) * mm, "end": v(-15.4, -25.42) * mm});
            skLineSegment(sketch, "E25.30.2.3", {"start": v(-15.4, -25.42) * mm, "end": v(-18.4, -27.15) * mm});
            skLineSegment(sketch, "E25.33.2.3", {"start": v(-21.4, -21.96) * mm, "end": v(-18.4, -20.22) * mm});
            skLineSegment(sketch, "E25.0.3.2", {"start": v(-15, -9.48) * mm, "end": v(-18, -7.75) * mm});
            skLineSegment(sketch, "E25.3.3.2", {"start": v(-18, -7.75) * mm, "end": v(-18, -4.29) * mm});
            skLineSegment(sketch, "E25.6.3.2", {"start": v(-18, -4.29) * mm, "end": v(-15, -2.56) * mm});
            skLineSegment(sketch, "E25.9.3.2", {"start": v(-15, -2.56) * mm, "end": v(-12, -4.29) * mm});
            skLineSegment(sketch, "E25.12.3.2", {"start": v(-12, -4.29) * mm, "end": v(-12, -7.75) * mm});
            skLineSegment(sketch, "E25.15.3.2", {"start": v(-12, -7.75) * mm, "end": v(-15, -9.48) * mm});
            skLineSegment(sketch, "E25.18.3.2", {"start": v(-11.6, -15.37) * mm, "end": v(-14.6, -13.64) * mm});
            skLineSegment(sketch, "E25.21.3.2", {"start": v(-14.6, -13.64) * mm, "end": v(-14.6, -10.18) * mm});
            skLineSegment(sketch, "E25.24.3.2", {"start": v(-11.6, -8.44) * mm, "end": v(-8.6, -10.18) * mm});
            skLineSegment(sketch, "E25.27.3.2", {"start": v(-8.6, -10.18) * mm, "end": v(-8.6, -13.64) * mm});
            skLineSegment(sketch, "E25.30.3.2", {"start": v(-8.6, -13.64) * mm, "end": v(-11.6, -15.37) * mm});
            skLineSegment(sketch, "E25.33.3.2", {"start": v(-14.6, -10.18) * mm, "end": v(-11.6, -8.44) * mm});
            skLineSegment(sketch, "E25.0.3.3", {"start": v(-15, -21.26) * mm, "end": v(-18, -19.53) * mm});
            skLineSegment(sketch, "E25.3.3.3", {"start": v(-18, -19.53) * mm, "end": v(-18, -16.07) * mm});
            skLineSegment(sketch, "E25.6.3.3", {"start": v(-18, -16.07) * mm, "end": v(-15, -14.33) * mm});
            skLineSegment(sketch, "E25.9.3.3", {"start": v(-15, -14.33) * mm, "end": v(-12, -16.07) * mm});
            skLineSegment(sketch, "E25.12.3.3", {"start": v(-12, -16.07) * mm, "end": v(-12, -19.53) * mm});
            skLineSegment(sketch, "E25.15.3.3", {"start": v(-12, -19.53) * mm, "end": v(-15, -21.26) * mm});
            skLineSegment(sketch, "E25.18.3.3", {"start": v(-11.6, -27.15) * mm, "end": v(-14.6, -25.42) * mm});
            skLineSegment(sketch, "E25.21.3.3", {"start": v(-14.6, -25.42) * mm, "end": v(-14.6, -21.96) * mm});
            skLineSegment(sketch, "E25.24.3.3", {"start": v(-11.6, -20.22) * mm, "end": v(-8.6, -21.96) * mm});
            skLineSegment(sketch, "E25.27.3.3", {"start": v(-8.6, -21.96) * mm, "end": v(-8.6, -25.42) * mm});
            skLineSegment(sketch, "E25.30.3.3", {"start": v(-8.6, -25.42) * mm, "end": v(-11.6, -27.15) * mm});
            skLineSegment(sketch, "E25.33.3.3", {"start": v(-14.6, -21.96) * mm, "end": v(-11.6, -20.22) * mm});
            skLineSegment(sketch, "E25.0.4.2", {"start": v(-8.2, -9.48) * mm, "end": v(-11.2, -7.75) * mm});
            skLineSegment(sketch, "E25.3.4.2", {"start": v(-11.2, -7.75) * mm, "end": v(-11.2, -4.29) * mm});
            skLineSegment(sketch, "E25.6.4.2", {"start": v(-11.2, -4.29) * mm, "end": v(-8.2, -2.56) * mm});
            skLineSegment(sketch, "E25.9.4.2", {"start": v(-8.2, -2.56) * mm, "end": v(-5.2, -4.29) * mm});
            skLineSegment(sketch, "E25.12.4.2", {"start": v(-5.2, -4.29) * mm, "end": v(-5.2, -7.75) * mm});
            skLineSegment(sketch, "E25.15.4.2", {"start": v(-5.2, -7.75) * mm, "end": v(-8.2, -9.48) * mm});
            skLineSegment(sketch, "E25.18.4.2", {"start": v(-4.8, -15.37) * mm, "end": v(-7.8, -13.64) * mm});
            skLineSegment(sketch, "E25.21.4.2", {"start": v(-7.8, -13.64) * mm, "end": v(-7.8, -10.18) * mm});
            skLineSegment(sketch, "E25.24.4.2", {"start": v(-4.8, -8.44) * mm, "end": v(-1.8, -10.18) * mm});
            skLineSegment(sketch, "E25.27.4.2", {"start": v(-1.8, -10.18) * mm, "end": v(-1.8, -13.64) * mm});
            skLineSegment(sketch, "E25.30.4.2", {"start": v(-1.8, -13.64) * mm, "end": v(-4.8, -15.37) * mm});
            skLineSegment(sketch, "E25.33.4.2", {"start": v(-7.8, -10.18) * mm, "end": v(-4.8, -8.44) * mm});
            skLineSegment(sketch, "E25.0.4.3", {"start": v(-8.2, -21.26) * mm, "end": v(-11.2, -19.53) * mm});
            skLineSegment(sketch, "E25.3.4.3", {"start": v(-11.2, -19.53) * mm, "end": v(-11.2, -16.07) * mm});
            skLineSegment(sketch, "E25.6.4.3", {"start": v(-11.2, -16.07) * mm, "end": v(-8.2, -14.33) * mm});
            skLineSegment(sketch, "E25.9.4.3", {"start": v(-8.2, -14.33) * mm, "end": v(-5.2, -16.07) * mm});
            skLineSegment(sketch, "E25.12.4.3", {"start": v(-5.2, -16.07) * mm, "end": v(-5.2, -19.53) * mm});
            skLineSegment(sketch, "E25.15.4.3", {"start": v(-5.2, -19.53) * mm, "end": v(-8.2, -21.26) * mm});
            skLineSegment(sketch, "E25.18.4.3", {"start": v(-4.8, -27.15) * mm, "end": v(-7.8, -25.42) * mm});
            skLineSegment(sketch, "E25.21.4.3", {"start": v(-7.8, -25.42) * mm, "end": v(-7.8, -21.96) * mm});
            skLineSegment(sketch, "E25.24.4.3", {"start": v(-4.8, -20.22) * mm, "end": v(-1.8, -21.96) * mm});
            skLineSegment(sketch, "E25.27.4.3", {"start": v(-1.8, -21.96) * mm, "end": v(-1.8, -25.42) * mm});
            skLineSegment(sketch, "E25.30.4.3", {"start": v(-1.8, -25.42) * mm, "end": v(-4.8, -27.15) * mm});
            skLineSegment(sketch, "E25.33.4.3", {"start": v(-7.8, -21.96) * mm, "end": v(-4.8, -20.22) * mm});
            skLineSegment(sketch, "E25.0.5.2", {"start": v(-1.4, -9.48) * mm, "end": v(-4.4, -7.75) * mm});
            skLineSegment(sketch, "E25.3.5.2", {"start": v(-4.4, -7.75) * mm, "end": v(-4.4, -4.29) * mm});
            skLineSegment(sketch, "E25.6.5.2", {"start": v(-4.4, -4.29) * mm, "end": v(-1.4, -2.56) * mm});
            skLineSegment(sketch, "E25.9.5.2", {"start": v(-1.4, -2.56) * mm, "end": v(1.6, -4.29) * mm});
            skLineSegment(sketch, "E25.12.5.2", {"start": v(1.6, -4.29) * mm, "end": v(1.6, -7.75) * mm});
            skLineSegment(sketch, "E25.15.5.2", {"start": v(1.6, -7.75) * mm, "end": v(-1.4, -9.48) * mm});
            skLineSegment(sketch, "E25.18.5.2", {"start": v(2, -15.37) * mm, "end": v(-1, -13.64) * mm});
            skLineSegment(sketch, "E25.21.5.2", {"start": v(-1, -13.64) * mm, "end": v(-1, -10.18) * mm});
            skLineSegment(sketch, "E25.24.5.2", {"start": v(2, -8.44) * mm, "end": v(5, -10.18) * mm});
            skLineSegment(sketch, "E25.27.5.2", {"start": v(5, -10.18) * mm, "end": v(5, -13.64) * mm});
            skLineSegment(sketch, "E25.30.5.2", {"start": v(5, -13.64) * mm, "end": v(2, -15.37) * mm});
            skLineSegment(sketch, "E25.33.5.2", {"start": v(-1, -10.18) * mm, "end": v(2, -8.44) * mm});
            skLineSegment(sketch, "E25.0.5.3", {"start": v(-1.4, -21.26) * mm, "end": v(-4.4, -19.53) * mm});
            skLineSegment(sketch, "E25.3.5.3", {"start": v(-4.4, -19.53) * mm, "end": v(-4.4, -16.07) * mm});
            skLineSegment(sketch, "E25.6.5.3", {"start": v(-4.4, -16.07) * mm, "end": v(-1.4, -14.33) * mm});
            skLineSegment(sketch, "E25.9.5.3", {"start": v(-1.4, -14.33) * mm, "end": v(1.6, -16.07) * mm});
            skLineSegment(sketch, "E25.12.5.3", {"start": v(1.6, -16.07) * mm, "end": v(1.6, -19.53) * mm});
            skLineSegment(sketch, "E25.15.5.3", {"start": v(1.6, -19.53) * mm, "end": v(-1.4, -21.26) * mm});
            skLineSegment(sketch, "E25.18.5.3", {"start": v(2, -27.15) * mm, "end": v(-1, -25.42) * mm});
            skLineSegment(sketch, "E25.21.5.3", {"start": v(-1, -25.42) * mm, "end": v(-1, -21.96) * mm});
            skLineSegment(sketch, "E25.24.5.3", {"start": v(2, -20.22) * mm, "end": v(5, -21.96) * mm});
            skLineSegment(sketch, "E25.27.5.3", {"start": v(5, -21.96) * mm, "end": v(5, -25.42) * mm});
            skLineSegment(sketch, "E25.30.5.3", {"start": v(5, -25.42) * mm, "end": v(2, -27.15) * mm});
            skLineSegment(sketch, "E25.33.5.3", {"start": v(-1, -21.96) * mm, "end": v(2, -20.22) * mm});
            skLineSegment(sketch, "E25.0.6.2", {"start": v(5.4, -9.48) * mm, "end": v(2.4, -7.75) * mm});
            skLineSegment(sketch, "E25.3.6.2", {"start": v(2.4, -7.75) * mm, "end": v(2.4, -4.29) * mm});
            skLineSegment(sketch, "E25.6.6.2", {"start": v(2.4, -4.29) * mm, "end": v(5.4, -2.56) * mm});
            skLineSegment(sketch, "E25.9.6.2", {"start": v(5.4, -2.56) * mm, "end": v(8.4, -4.29) * mm});
            skLineSegment(sketch, "E25.12.6.2", {"start": v(8.4, -4.29) * mm, "end": v(8.4, -7.75) * mm});
            skLineSegment(sketch, "E25.15.6.2", {"start": v(8.4, -7.75) * mm, "end": v(5.4, -9.48) * mm});
            skLineSegment(sketch, "E25.18.6.2", {"start": v(8.8, -15.37) * mm, "end": v(5.8, -13.64) * mm});
            skLineSegment(sketch, "E25.21.6.2", {"start": v(5.8, -13.64) * mm, "end": v(5.8, -10.18) * mm});
            skLineSegment(sketch, "E25.24.6.2", {"start": v(8.8, -8.44) * mm, "end": v(11.8, -10.18) * mm});
            skLineSegment(sketch, "E25.27.6.2", {"start": v(11.8, -10.18) * mm, "end": v(11.8, -13.64) * mm});
            skLineSegment(sketch, "E25.30.6.2", {"start": v(11.8, -13.64) * mm, "end": v(8.8, -15.37) * mm});
            skLineSegment(sketch, "E25.33.6.2", {"start": v(5.8, -10.18) * mm, "end": v(8.8, -8.44) * mm});
            skLineSegment(sketch, "E25.0.6.3", {"start": v(5.4, -21.26) * mm, "end": v(2.4, -19.53) * mm});
            skLineSegment(sketch, "E25.3.6.3", {"start": v(2.4, -19.53) * mm, "end": v(2.4, -16.07) * mm});
            skLineSegment(sketch, "E25.6.6.3", {"start": v(2.4, -16.07) * mm, "end": v(5.4, -14.33) * mm});
            skLineSegment(sketch, "E25.9.6.3", {"start": v(5.4, -14.33) * mm, "end": v(8.4, -16.07) * mm});
            skLineSegment(sketch, "E25.12.6.3", {"start": v(8.4, -16.07) * mm, "end": v(8.4, -19.53) * mm});
            skLineSegment(sketch, "E25.15.6.3", {"start": v(8.4, -19.53) * mm, "end": v(5.4, -21.26) * mm});
            skLineSegment(sketch, "E25.18.6.3", {"start": v(8.8, -27.15) * mm, "end": v(5.8, -25.42) * mm});
            skLineSegment(sketch, "E25.21.6.3", {"start": v(5.8, -25.42) * mm, "end": v(5.8, -21.96) * mm});
            skLineSegment(sketch, "E25.24.6.3", {"start": v(8.8, -20.22) * mm, "end": v(11.8, -21.96) * mm});
            skLineSegment(sketch, "E25.27.6.3", {"start": v(11.8, -21.96) * mm, "end": v(11.8, -25.42) * mm});
            skLineSegment(sketch, "E25.30.6.3", {"start": v(11.8, -25.42) * mm, "end": v(8.8, -27.15) * mm});
            skLineSegment(sketch, "E25.33.6.3", {"start": v(5.8, -21.96) * mm, "end": v(8.8, -20.22) * mm});
            skLineSegment(sketch, "E25.0.7.2", {"start": v(12.2, -9.48) * mm, "end": v(9.2, -7.75) * mm});
            skLineSegment(sketch, "E25.3.7.2", {"start": v(9.2, -7.75) * mm, "end": v(9.2, -4.29) * mm});
            skLineSegment(sketch, "E25.6.7.2", {"start": v(9.2, -4.29) * mm, "end": v(12.2, -2.56) * mm});
            skLineSegment(sketch, "E25.9.7.2", {"start": v(12.2, -2.56) * mm, "end": v(15.2, -4.29) * mm});
            skLineSegment(sketch, "E25.12.7.2", {"start": v(15.2, -4.29) * mm, "end": v(15.2, -7.75) * mm});
            skLineSegment(sketch, "E25.15.7.2", {"start": v(15.2, -7.75) * mm, "end": v(12.2, -9.48) * mm});
            skLineSegment(sketch, "E25.18.7.2", {"start": v(15.6, -15.37) * mm, "end": v(12.6, -13.64) * mm});
            skLineSegment(sketch, "E25.21.7.2", {"start": v(12.6, -13.64) * mm, "end": v(12.6, -10.18) * mm});
            skLineSegment(sketch, "E25.24.7.2", {"start": v(15.6, -8.44) * mm, "end": v(18.6, -10.18) * mm});
            skLineSegment(sketch, "E25.27.7.2", {"start": v(18.6, -10.18) * mm, "end": v(18.6, -13.64) * mm});
            skLineSegment(sketch, "E25.30.7.2", {"start": v(18.6, -13.64) * mm, "end": v(15.6, -15.37) * mm});
            skLineSegment(sketch, "E25.33.7.2", {"start": v(12.6, -10.18) * mm, "end": v(15.6, -8.44) * mm});
            skLineSegment(sketch, "E25.0.7.3", {"start": v(12.2, -21.26) * mm, "end": v(9.2, -19.53) * mm});
            skLineSegment(sketch, "E25.3.7.3", {"start": v(9.2, -19.53) * mm, "end": v(9.2, -16.07) * mm});
            skLineSegment(sketch, "E25.6.7.3", {"start": v(9.2, -16.07) * mm, "end": v(12.2, -14.33) * mm});
            skLineSegment(sketch, "E25.9.7.3", {"start": v(12.2, -14.33) * mm, "end": v(15.2, -16.07) * mm});
            skLineSegment(sketch, "E25.12.7.3", {"start": v(15.2, -16.07) * mm, "end": v(15.2, -19.53) * mm});
            skLineSegment(sketch, "E25.15.7.3", {"start": v(15.2, -19.53) * mm, "end": v(12.2, -21.26) * mm});
            skLineSegment(sketch, "E25.18.7.3", {"start": v(15.6, -27.15) * mm, "end": v(12.6, -25.42) * mm});
            skLineSegment(sketch, "E25.21.7.3", {"start": v(12.6, -25.42) * mm, "end": v(12.6, -21.96) * mm});
            skLineSegment(sketch, "E25.24.7.3", {"start": v(15.6, -20.22) * mm, "end": v(18.6, -21.96) * mm});
            skLineSegment(sketch, "E25.27.7.3", {"start": v(18.6, -21.96) * mm, "end": v(18.6, -25.42) * mm});
            skLineSegment(sketch, "E25.30.7.3", {"start": v(18.6, -25.42) * mm, "end": v(15.6, -27.15) * mm});
            skLineSegment(sketch, "E25.33.7.3", {"start": v(12.6, -21.96) * mm, "end": v(15.6, -20.22) * mm});
            skLineSegment(sketch, "E25.0.8.2", {"start": v(19, -9.48) * mm, "end": v(16, -7.75) * mm});
            skLineSegment(sketch, "E25.3.8.2", {"start": v(16, -7.75) * mm, "end": v(16, -4.29) * mm});
            skLineSegment(sketch, "E25.6.8.2", {"start": v(16, -4.29) * mm, "end": v(19, -2.56) * mm});
            skLineSegment(sketch, "E25.9.8.2", {"start": v(19, -2.56) * mm, "end": v(22, -4.29) * mm});
            skLineSegment(sketch, "E25.12.8.2", {"start": v(22, -4.29) * mm, "end": v(22, -7.75) * mm});
            skLineSegment(sketch, "E25.15.8.2", {"start": v(22, -7.75) * mm, "end": v(19, -9.48) * mm});
            skLineSegment(sketch, "E25.18.8.2", {"start": v(22.4, -15.37) * mm, "end": v(19.4, -13.64) * mm});
            skLineSegment(sketch, "E25.21.8.2", {"start": v(19.4, -13.64) * mm, "end": v(19.4, -10.18) * mm});
            skLineSegment(sketch, "E25.24.8.2", {"start": v(22.4, -8.44) * mm, "end": v(25.4, -10.18) * mm});
            skLineSegment(sketch, "E25.27.8.2", {"start": v(25.4, -10.18) * mm, "end": v(25.4, -13.64) * mm});
            skLineSegment(sketch, "E25.30.8.2", {"start": v(25.4, -13.64) * mm, "end": v(22.4, -15.37) * mm});
            skLineSegment(sketch, "E25.33.8.2", {"start": v(19.4, -10.18) * mm, "end": v(22.4, -8.44) * mm});
            skLineSegment(sketch, "E25.0.8.3", {"start": v(19, -21.26) * mm, "end": v(16, -19.53) * mm});
            skLineSegment(sketch, "E25.3.8.3", {"start": v(16, -19.53) * mm, "end": v(16, -16.07) * mm});
            skLineSegment(sketch, "E25.6.8.3", {"start": v(16, -16.07) * mm, "end": v(19, -14.33) * mm});
            skLineSegment(sketch, "E25.9.8.3", {"start": v(19, -14.33) * mm, "end": v(22, -16.07) * mm});
            skLineSegment(sketch, "E25.12.8.3", {"start": v(22, -16.07) * mm, "end": v(22, -19.53) * mm});
            skLineSegment(sketch, "E25.15.8.3", {"start": v(22, -19.53) * mm, "end": v(19, -21.26) * mm});
            skLineSegment(sketch, "E25.18.8.3", {"start": v(22.4, -27.15) * mm, "end": v(19.4, -25.42) * mm});
            skLineSegment(sketch, "E25.21.8.3", {"start": v(19.4, -25.42) * mm, "end": v(19.4, -21.96) * mm});
            skLineSegment(sketch, "E25.24.8.3", {"start": v(22.4, -20.22) * mm, "end": v(25.4, -21.96) * mm});
            skLineSegment(sketch, "E25.27.8.3", {"start": v(25.4, -21.96) * mm, "end": v(25.4, -25.42) * mm});
            skLineSegment(sketch, "E25.30.8.3", {"start": v(25.4, -25.42) * mm, "end": v(22.4, -27.15) * mm});
            skLineSegment(sketch, "E25.33.8.3", {"start": v(19.4, -21.96) * mm, "end": v(22.4, -20.22) * mm});
            skLineSegment(sketch, "E25.0.9.2", {"start": v(25.8, -9.48) * mm, "end": v(22.8, -7.75) * mm});
            skLineSegment(sketch, "E25.3.9.2", {"start": v(22.8, -7.75) * mm, "end": v(22.8, -4.29) * mm});
            skLineSegment(sketch, "E25.6.9.2", {"start": v(22.8, -4.29) * mm, "end": v(25.8, -2.56) * mm});
            skLineSegment(sketch, "E25.9.9.2", {"start": v(25.8, -2.56) * mm, "end": v(28.8, -4.29) * mm});
            skLineSegment(sketch, "E25.12.9.2", {"start": v(28.8, -4.29) * mm, "end": v(28.8, -7.75) * mm});
            skLineSegment(sketch, "E25.15.9.2", {"start": v(28.8, -7.75) * mm, "end": v(25.8, -9.48) * mm});
            skLineSegment(sketch, "E25.18.9.2", {"start": v(29.2, -15.37) * mm, "end": v(26.2, -13.64) * mm});
            skLineSegment(sketch, "E25.21.9.2", {"start": v(26.2, -13.64) * mm, "end": v(26.2, -10.18) * mm});
            skLineSegment(sketch, "E25.24.9.2", {"start": v(29.2, -8.44) * mm, "end": v(32.2, -10.18) * mm});
            skLineSegment(sketch, "E25.27.9.2", {"start": v(32.2, -10.18) * mm, "end": v(32.2, -13.64) * mm});
            skLineSegment(sketch, "E25.30.9.2", {"start": v(32.2, -13.64) * mm, "end": v(29.2, -15.37) * mm});
            skLineSegment(sketch, "E25.33.9.2", {"start": v(26.2, -10.18) * mm, "end": v(29.2, -8.44) * mm});
            skLineSegment(sketch, "E25.0.9.3", {"start": v(25.8, -21.26) * mm, "end": v(22.8, -19.53) * mm});
            skLineSegment(sketch, "E25.3.9.3", {"start": v(22.8, -19.53) * mm, "end": v(22.8, -16.07) * mm});
            skLineSegment(sketch, "E25.6.9.3", {"start": v(22.8, -16.07) * mm, "end": v(25.8, -14.33) * mm});
            skLineSegment(sketch, "E25.9.9.3", {"start": v(25.8, -14.33) * mm, "end": v(28.8, -16.07) * mm});
            skLineSegment(sketch, "E25.12.9.3", {"start": v(28.8, -16.07) * mm, "end": v(28.8, -19.53) * mm});
            skLineSegment(sketch, "E25.15.9.3", {"start": v(28.8, -19.53) * mm, "end": v(25.8, -21.26) * mm});
            skLineSegment(sketch, "E25.18.9.3", {"start": v(29.2, -27.15) * mm, "end": v(26.2, -25.42) * mm});
            skLineSegment(sketch, "E25.21.9.3", {"start": v(26.2, -25.42) * mm, "end": v(26.2, -21.96) * mm});
            skLineSegment(sketch, "E25.24.9.3", {"start": v(29.2, -20.22) * mm, "end": v(32.2, -21.96) * mm});
            skLineSegment(sketch, "E25.27.9.3", {"start": v(32.2, -21.96) * mm, "end": v(32.2, -25.42) * mm});
            skLineSegment(sketch, "E25.30.9.3", {"start": v(32.2, -25.42) * mm, "end": v(29.2, -27.15) * mm});
            skLineSegment(sketch, "E25.33.9.3", {"start": v(26.2, -21.96) * mm, "end": v(29.2, -20.22) * mm});
            skLineSegment(sketch, "E25.0.10.2", {"start": v(32.6, -9.48) * mm, "end": v(29.6, -7.75) * mm});
            skLineSegment(sketch, "E25.3.10.2", {"start": v(29.6, -7.75) * mm, "end": v(29.6, -4.29) * mm});
            skLineSegment(sketch, "E25.6.10.2", {"start": v(29.6, -4.29) * mm, "end": v(32.6, -2.56) * mm});
            skLineSegment(sketch, "E25.9.10.2", {"start": v(32.6, -2.56) * mm, "end": v(35.6, -4.29) * mm});
            skLineSegment(sketch, "E25.12.10.2", {"start": v(35.6, -4.29) * mm, "end": v(35.6, -7.75) * mm});
            skLineSegment(sketch, "E25.15.10.2", {"start": v(35.6, -7.75) * mm, "end": v(32.6, -9.48) * mm});
            skLineSegment(sketch, "E25.18.10.2", {"start": v(36, -15.37) * mm, "end": v(33, -13.64) * mm});
            skLineSegment(sketch, "E25.21.10.2", {"start": v(33, -13.64) * mm, "end": v(33, -10.18) * mm});
            skLineSegment(sketch, "E25.24.10.2", {"start": v(36, -8.44) * mm, "end": v(39, -10.18) * mm});
            skLineSegment(sketch, "E25.27.10.2", {"start": v(39, -10.18) * mm, "end": v(39, -13.64) * mm});
            skLineSegment(sketch, "E25.30.10.2", {"start": v(39, -13.64) * mm, "end": v(36, -15.37) * mm});
            skLineSegment(sketch, "E25.33.10.2", {"start": v(33, -10.18) * mm, "end": v(36, -8.44) * mm});
            skLineSegment(sketch, "E25.0.10.3", {"start": v(32.6, -21.26) * mm, "end": v(29.6, -19.53) * mm});
            skLineSegment(sketch, "E25.3.10.3", {"start": v(29.6, -19.53) * mm, "end": v(29.6, -16.07) * mm});
            skLineSegment(sketch, "E25.6.10.3", {"start": v(29.6, -16.07) * mm, "end": v(32.6, -14.33) * mm});
            skLineSegment(sketch, "E25.9.10.3", {"start": v(32.6, -14.33) * mm, "end": v(35.6, -16.07) * mm});
            skLineSegment(sketch, "E25.12.10.3", {"start": v(35.6, -16.07) * mm, "end": v(35.6, -19.53) * mm});
            skLineSegment(sketch, "E25.15.10.3", {"start": v(35.6, -19.53) * mm, "end": v(32.6, -21.26) * mm});
            skLineSegment(sketch, "E25.18.10.3", {"start": v(36, -27.15) * mm, "end": v(33, -25.42) * mm});
            skLineSegment(sketch, "E25.21.10.3", {"start": v(33, -25.42) * mm, "end": v(33, -21.96) * mm});
            skLineSegment(sketch, "E25.24.10.3", {"start": v(36, -20.22) * mm, "end": v(39, -21.96) * mm});
            skLineSegment(sketch, "E25.27.10.3", {"start": v(39, -21.96) * mm, "end": v(39, -25.42) * mm});
            skLineSegment(sketch, "E25.30.10.3", {"start": v(39, -25.42) * mm, "end": v(36, -27.15) * mm});
            skLineSegment(sketch, "E25.33.10.3", {"start": v(33, -21.96) * mm, "end": v(36, -20.22) * mm});
            skLineSegment(sketch, "E25.0.11.2", {"start": v(39.4, -9.48) * mm, "end": v(36.4, -7.75) * mm});
            skLineSegment(sketch, "E25.3.11.2", {"start": v(36.4, -7.75) * mm, "end": v(36.4, -4.29) * mm});
            skLineSegment(sketch, "E25.6.11.2", {"start": v(36.4, -4.29) * mm, "end": v(39.4, -2.56) * mm});
            skLineSegment(sketch, "E25.9.11.2", {"start": v(39.4, -2.56) * mm, "end": v(42.4, -4.29) * mm});
            skLineSegment(sketch, "E25.12.11.2", {"start": v(42.4, -4.29) * mm, "end": v(42.4, -7.75) * mm});
            skLineSegment(sketch, "E25.15.11.2", {"start": v(42.4, -7.75) * mm, "end": v(39.4, -9.48) * mm});
            skLineSegment(sketch, "E25.18.11.2", {"start": v(42.8, -15.37) * mm, "end": v(39.8, -13.64) * mm});
            skLineSegment(sketch, "E25.21.11.2", {"start": v(39.8, -13.64) * mm, "end": v(39.8, -10.18) * mm});
            skLineSegment(sketch, "E25.24.11.2", {"start": v(42.8, -8.44) * mm, "end": v(45.8, -10.18) * mm});
            skLineSegment(sketch, "E25.27.11.2", {"start": v(45.8, -10.18) * mm, "end": v(45.8, -13.64) * mm});
            skLineSegment(sketch, "E25.30.11.2", {"start": v(45.8, -13.64) * mm, "end": v(42.8, -15.37) * mm});
            skLineSegment(sketch, "E25.33.11.2", {"start": v(39.8, -10.18) * mm, "end": v(42.8, -8.44) * mm});
            skLineSegment(sketch, "E25.0.11.3", {"start": v(39.4, -21.26) * mm, "end": v(36.4, -19.53) * mm});
            skLineSegment(sketch, "E25.3.11.3", {"start": v(36.4, -19.53) * mm, "end": v(36.4, -16.07) * mm});
            skLineSegment(sketch, "E25.6.11.3", {"start": v(36.4, -16.07) * mm, "end": v(39.4, -14.33) * mm});
            skLineSegment(sketch, "E25.9.11.3", {"start": v(39.4, -14.33) * mm, "end": v(42.4, -16.07) * mm});
            skLineSegment(sketch, "E25.12.11.3", {"start": v(42.4, -16.07) * mm, "end": v(42.4, -19.53) * mm});
            skLineSegment(sketch, "E25.15.11.3", {"start": v(42.4, -19.53) * mm, "end": v(39.4, -21.26) * mm});
            skLineSegment(sketch, "E25.18.11.3", {"start": v(42.8, -27.15) * mm, "end": v(39.8, -25.42) * mm});
            skLineSegment(sketch, "E25.21.11.3", {"start": v(39.8, -25.42) * mm, "end": v(39.8, -21.96) * mm});
            skLineSegment(sketch, "E25.24.11.3", {"start": v(42.8, -20.22) * mm, "end": v(45.8, -21.96) * mm});
            skLineSegment(sketch, "E25.27.11.3", {"start": v(45.8, -21.96) * mm, "end": v(45.8, -25.42) * mm});
            skLineSegment(sketch, "E25.30.11.3", {"start": v(45.8, -25.42) * mm, "end": v(42.8, -27.15) * mm});
            skLineSegment(sketch, "E25.33.11.3", {"start": v(39.8, -21.96) * mm, "end": v(42.8, -20.22) * mm});
            skSolve(sketch);
        }
        {
            var Q0;
            Q0=makeQuery(id+"F5.imprint","IMPRINT",FACE,{"disambiguationData":[TD([[makeQuery(id+"F5.imprint","IMPRINT",EDGE,{"derivedFrom":sQuery(id+"F5.wireOp",EDGE,"E24.18.6.1")}),-1.0]])]});
            var Q1;
            Q1=makeQuery(id+"F5.imprint","IMPRINT",FACE,{"disambiguationData":[TD([[makeQuery(id+"F5.imprint","IMPRINT",EDGE,{"derivedFrom":sQuery(id+"F5.wireOp",EDGE,"E24.0.2.1")}),-1.0]])]});
            var Q2;
            Q2=makeQuery(id+"F5.imprint","IMPRINT",FACE,{"disambiguationData":[TD([[makeQuery(id+"F5.imprint","IMPRINT",EDGE,{"derivedFrom":sQuery(id+"F5.wireOp",EDGE,"E25.0.6.3")}),-1.0]])]});
            var Q3;
            Q3=makeQuery(id+"F5.imprint","IMPRINT",FACE,{"disambiguationData":[TD([[makeQuery(id+"F5.imprint","IMPRINT",EDGE,{"derivedFrom":sQuery(id+"F5.wireOp",EDGE,"E25.0.2.3")}),-1.0]])]});
            var Q4;
            Q4=makeQuery(id+"F5.imprint","IMPRINT",FACE,{"disambiguationData":[TD([[makeQuery(id+"F5.imprint","IMPRINT",EDGE,{"derivedFrom":sQuery(id+"F5.wireOp",EDGE,"E24.0.10.1")}),-1.0]])]});
            var Q5;
            Q5=makeQuery(id+"F5.imprint","IMPRINT",FACE,{"disambiguationData":[TD([[makeQuery(id+"F5.imprint","IMPRINT",EDGE,{"derivedFrom":sQuery(id+"F5.wireOp",EDGE,"E25.0.7.2")}),-1.0]])]});
            var Q6;
            Q6=makeQuery(id+"F5.imprint","IMPRINT",FACE,{"disambiguationData":[TD([[makeQuery(id+"F5.imprint","IMPRINT",EDGE,{"derivedFrom":sQuery(id+"F5.wireOp",EDGE,"E25.0.3.2")}),-1.0]])]});
            var Q7;
            Q7=makeQuery(id+"F5.imprint","IMPRINT",FACE,{"disambiguationData":[TD([[makeQuery(id+"F5.imprint","IMPRINT",EDGE,{"derivedFrom":sQuery(id+"F5.wireOp",EDGE,"E25.0.11.2")}),-1.0]])]});
            var Q8;
            Q8=makeQuery(id+"F5.imprint","IMPRINT",FACE,{"disambiguationData":[TD([[makeQuery(id+"F5.imprint","IMPRINT",EDGE,{"derivedFrom":sQuery(id+"F5.wireOp",EDGE,"E24.18.9.1")}),-1.0]])]});
            var Q9;
            Q9=makeQuery(id+"F5.imprint","IMPRINT",FACE,{"disambiguationData":[TD([[makeQuery(id+"F5.imprint","IMPRINT",EDGE,{"derivedFrom":sQuery(id+"F5.wireOp",EDGE,"E25.18.6.3")}),-1.0]])]});
            var Q10;
            Q10=makeQuery(id+"F5.imprint","IMPRINT",FACE,{"disambiguationData":[TD([[makeQuery(id+"F5.imprint","IMPRINT",EDGE,{"derivedFrom":sQuery(id+"F5.wireOp",EDGE,"E25.18.2.3")}),-1.0]])]});
            var Q11;
            Q11=makeQuery(id+"F5.imprint","IMPRINT",FACE,{"disambiguationData":[TD([[makeQuery(id+"F5.imprint","IMPRINT",EDGE,{"derivedFrom":sQuery(id+"F5.wireOp",EDGE,"E25.18.10.3")}),-1.0]])]});
            var Q12;
            Q12=makeQuery(id+"F5.imprint","IMPRINT",FACE,{"disambiguationData":[TD([[makeQuery(id+"F5.imprint","IMPRINT",EDGE,{"derivedFrom":sQuery(id+"F5.wireOp",EDGE,"E24.18.1.1")}),-1.0]])]});
            var Q13;
            Q13=makeQuery(id+"F5.imprint","IMPRINT",FACE,{"disambiguationData":[TD([[makeQuery(id+"F5.imprint","IMPRINT",EDGE,{"derivedFrom":sQuery(id+"F5.wireOp",EDGE,"E25.0.10.3")}),-1.0]])]});
            var Q14;
            Q14=makeQuery(id+"F5.imprint","IMPRINT",FACE,{"disambiguationData":[TD([[makeQuery(id+"F5.imprint","IMPRINT",EDGE,{"derivedFrom":sQuery(id+"F5.wireOp",EDGE,"E24.0.9.1")}),-1.0]])]});
            var Q15;
            Q15=makeQuery(id+"F5.imprint","IMPRINT",FACE,{"disambiguationData":[TD([[makeQuery(id+"F5.imprint","IMPRINT",EDGE,{"derivedFrom":sQuery(id+"F5.wireOp",EDGE,"E24.0.1.1")}),-1.0]])]});
            var Q16;
            Q16=makeQuery(id+"F5.imprint","IMPRINT",FACE,{"disambiguationData":[TD([[makeQuery(id+"F5.imprint","IMPRINT",EDGE,{"derivedFrom":sQuery(id+"F5.wireOp",EDGE,"E25.18.2.2")}),-1.0]])]});
            var Q17;
            Q17=makeQuery(id+"F5.imprint","IMPRINT",FACE,{"disambiguationData":[TD([[makeQuery(id+"F5.imprint","IMPRINT",EDGE,{"derivedFrom":sQuery(id+"F5.wireOp",EDGE,"E24.18.0.1")}),-1.0]])]});
            var Q18;
            Q18=makeQuery(id+"F5.imprint","IMPRINT",FACE,{"disambiguationData":[TD([[makeQuery(id+"F5.imprint","IMPRINT",EDGE,{"derivedFrom":sQuery(id+"F5.wireOp",EDGE,"E24.0.8.1")}),-1.0]])]});
            var Q19;
            Q19=makeQuery(id+"F5.imprint","IMPRINT",FACE,{"disambiguationData":[TD([[makeQuery(id+"F5.imprint","IMPRINT",EDGE,{"derivedFrom":sQuery(id+"F5.wireOp",EDGE,"E25.0.6.2")}),-1.0]])]});
            var Q20;
            Q20=makeQuery(id+"F5.imprint","IMPRINT",FACE,{"disambiguationData":[TD([[makeQuery(id+"F5.imprint","IMPRINT",EDGE,{"derivedFrom":sQuery(id+"F5.wireOp",EDGE,"E25.0.2.2")}),-1.0]])]});
            var Q21;
            Q21=makeQuery(id+"F5.imprint","IMPRINT",FACE,{"disambiguationData":[TD([[makeQuery(id+"F5.imprint","IMPRINT",EDGE,{"derivedFrom":sQuery(id+"F5.wireOp",EDGE,"E25.0.10.2")}),-1.0]])]});
            var Q22;
            Q22=makeQuery(id+"F5.imprint","IMPRINT",FACE,{"disambiguationData":[TD([[makeQuery(id+"F5.imprint","IMPRINT",EDGE,{"derivedFrom":sQuery(id+"F5.wireOp",EDGE,"E24.0.0.1")}),-1.0]])]});
            var Q23;
            Q23=makeQuery(id+"F5.imprint","IMPRINT",FACE,{"disambiguationData":[TD([[makeQuery(id+"F5.imprint","IMPRINT",EDGE,{"derivedFrom":sQuery(id+"F5.wireOp",EDGE,"E24.18.7.1")}),-1.0]])]});
            var Q24;
            Q24=makeQuery(id+"F5.imprint","IMPRINT",FACE,{"disambiguationData":[TD([[makeQuery(id+"F5.imprint","IMPRINT",EDGE,{"derivedFrom":sQuery(id+"F5.wireOp",EDGE,"E25.18.1.3")}),-1.0]])]});
            var Q25;
            Q25=makeQuery(id+"F5.imprint","IMPRINT",FACE,{"disambiguationData":[TD([[makeQuery(id+"F5.imprint","IMPRINT",EDGE,{"derivedFrom":sQuery(id+"F5.wireOp",EDGE,"E25.18.5.3")}),-1.0]])]});
            var Q26;
            Q26=makeQuery(id+"F5.imprint","IMPRINT",FACE,{"disambiguationData":[TD([[makeQuery(id+"F5.imprint","IMPRINT",EDGE,{"derivedFrom":sQuery(id+"F5.wireOp",EDGE,"E23.11.0.0")}),-1.0]])]});
            var Q27;
            Q27=makeQuery(id+"F5.imprint","IMPRINT",FACE,{"disambiguationData":[TD([[makeQuery(id+"F5.imprint","IMPRINT",EDGE,{"derivedFrom":sQuery(id+"F5.wireOp",EDGE,"E24.0.7.1")}),-1.0]])]});
            var Q28;
            Q28=makeQuery(id+"F5.imprint","IMPRINT",FACE,{"disambiguationData":[TD([[makeQuery(id+"F5.imprint","IMPRINT",EDGE,{"derivedFrom":sQuery(id+"F5.wireOp",EDGE,"E25.0.1.3")}),-1.0]])]});
            var Q29;
            Q29=makeQuery(id+"F5.imprint","IMPRINT",FACE,{"disambiguationData":[TD([[makeQuery(id+"F5.imprint","IMPRINT",EDGE,{"derivedFrom":sQuery(id+"F5.wireOp",EDGE,"E25.0.9.3")}),-1.0]])]});
            var Q30;
            Q30=makeQuery(id+"F5.imprint","IMPRINT",FACE,{"disambiguationData":[TD([[makeQuery(id+"F5.imprint","IMPRINT",EDGE,{"derivedFrom":sQuery(id+"F5.wireOp",EDGE,"E25.18.5.2")}),-1.0]])]});
            var Q31;
            Q31=makeQuery(id+"F5.imprint","IMPRINT",FACE,{"disambiguationData":[TD([[makeQuery(id+"F5.imprint","IMPRINT",EDGE,{"derivedFrom":sQuery(id+"F5.wireOp",EDGE,"E25.18.9.2")}),-1.0]])]});
            var Q32;
            Q32=makeQuery(id+"F5.imprint","IMPRINT",FACE,{"disambiguationData":[TD([[makeQuery(id+"F5.imprint","IMPRINT",EDGE,{"derivedFrom":sQuery(id+"F5.wireOp",EDGE,"E23.10.0.6")}),-1.0]])]});
            var Q33;
            Q33=makeQuery(id+"F5.imprint","IMPRINT",FACE,{"disambiguationData":[TD([[makeQuery(id+"F5.imprint","IMPRINT",EDGE,{"derivedFrom":sQuery(id+"F5.wireOp",EDGE,"E25.18.1.2")}),-1.0]])]});
            var Q34;
            Q34=makeQuery(id+"F5.imprint","IMPRINT",FACE,{"disambiguationData":[TD([[makeQuery(id+"F5.imprint","IMPRINT",EDGE,{"derivedFrom":sQuery(id+"F5.wireOp",EDGE,"E25.0.5.2")}),-1.0]])]});
            var Q35;
            Q35=makeQuery(id+"F5.imprint","IMPRINT",FACE,{"disambiguationData":[TD([[makeQuery(id+"F5.imprint","IMPRINT",EDGE,{"derivedFrom":sQuery(id+"F5.wireOp",EDGE,"E25.0.9.2")}),-1.0]])]});
            var Q36;
            Q36=makeQuery(id+"F5.imprint","IMPRINT",FACE,{"disambiguationData":[TD([[makeQuery(id+"F5.imprint","IMPRINT",EDGE,{"derivedFrom":sQuery(id+"F5.wireOp",EDGE,"E25.0.1.2")}),-1.0]])]});
            var Q37;
            Q37=makeQuery(id+"F5.imprint","IMPRINT",FACE,{"disambiguationData":[TD([[makeQuery(id+"F5.imprint","IMPRINT",EDGE,{"derivedFrom":sQuery(id+"F5.wireOp",EDGE,"E23.10.0.0")}),-1.0]])]});
            var Q38;
            Q38=makeQuery(id+"F5.imprint","IMPRINT",FACE,{"disambiguationData":[TD([[makeQuery(id+"F5.imprint","IMPRINT",EDGE,{"derivedFrom":sQuery(id+"F5.wireOp",EDGE,"E24.0.6.1")}),-1.0]])]});
            var Q39;
            Q39=makeQuery(id+"F5.imprint","IMPRINT",FACE,{"disambiguationData":[TD([[makeQuery(id+"F5.imprint","IMPRINT",EDGE,{"derivedFrom":sQuery(id+"F5.wireOp",EDGE,"E24.18.8.1")}),-1.0]])]});
            var Q40;
            Q40=makeQuery(id+"F5.imprint","IMPRINT",FACE,{"disambiguationData":[TD([[makeQuery(id+"F5.imprint","IMPRINT",EDGE,{"derivedFrom":sQuery(id+"F5.wireOp",EDGE,"E25.18.6.2")}),-1.0]])]});
            var Q41;
            Q41=makeQuery(id+"F5.imprint","IMPRINT",FACE,{"disambiguationData":[TD([[makeQuery(id+"F5.imprint","IMPRINT",EDGE,{"derivedFrom":sQuery(id+"F5.wireOp",EDGE,"E25.18.10.2")}),-1.0]])]});
            var Q42;
            Q42=makeQuery(id+"F5.imprint","IMPRINT",FACE,{"disambiguationData":[TD([[makeQuery(id+"F5.imprint","IMPRINT",EDGE,{"derivedFrom":sQuery(id+"F5.wireOp",EDGE,"E25.18.4.3")}),-1.0]])]});
            var Q43;
            Q43=makeQuery(id+"F5.imprint","IMPRINT",FACE,{"disambiguationData":[TD([[makeQuery(id+"F5.imprint","IMPRINT",EDGE,{"derivedFrom":sQuery(id+"F5.wireOp",EDGE,"E25.18.9.3")}),-1.0]])]});
            var Q44;
            Q44=makeQuery(id+"F5.imprint","IMPRINT",FACE,{"disambiguationData":[TD([[makeQuery(id+"F5.imprint","IMPRINT",EDGE,{"derivedFrom":sQuery(id+"F5.wireOp",EDGE,"E25.18.8.3")}),-1.0]])]});
            var Q45;
            Q45=makeQuery(id+"F5.imprint","IMPRINT",FACE,{"disambiguationData":[TD([[makeQuery(id+"F5.imprint","IMPRINT",EDGE,{"derivedFrom":sQuery(id+"F5.wireOp",EDGE,"E25.18.0.3")}),-1.0]])]});
            var Q46;
            Q46=makeQuery(id+"F5.imprint","IMPRINT",FACE,{"disambiguationData":[TD([[makeQuery(id+"F5.imprint","IMPRINT",EDGE,{"derivedFrom":sQuery(id+"F5.wireOp",EDGE,"E23.9.0.6")}),-1.0]])]});
            var Q47;
            Q47=makeQuery(id+"F5.imprint","IMPRINT",FACE,{"disambiguationData":[TD([[makeQuery(id+"F5.imprint","IMPRINT",EDGE,{"derivedFrom":sQuery(id+"F5.wireOp",EDGE,"E24.18.5.1")}),-1.0]])]});
            var Q48;
            Q48=makeQuery(id+"F5.imprint","IMPRINT",FACE,{"disambiguationData":[TD([[makeQuery(id+"F5.imprint","IMPRINT",EDGE,{"derivedFrom":sQuery(id+"F5.wireOp",EDGE,"E23.11.0.6")}),-1.0]])]});
            var Q49;
            Q49=makeQuery(id+"F5.imprint","IMPRINT",FACE,{"disambiguationData":[TD([[makeQuery(id+"F5.imprint","IMPRINT",EDGE,{"derivedFrom":sQuery(id+"F5.wireOp",EDGE,"E25.0.5.3")}),-1.0]])]});
            var Q50;
            Q50=makeQuery(id+"F5.imprint","IMPRINT",FACE,{"disambiguationData":[TD([[makeQuery(id+"F5.imprint","IMPRINT",EDGE,{"derivedFrom":sQuery(id+"F5.wireOp",EDGE,"E25.0.4.3")}),-1.0]])]});
            var Q51;
            Q51=makeQuery(id+"F5.imprint","IMPRINT",FACE,{"disambiguationData":[TD([[makeQuery(id+"F5.imprint","IMPRINT",EDGE,{"derivedFrom":sQuery(id+"F5.wireOp",EDGE,"E25.0.8.3")}),-1.0]])]});
            var Q52;
            Q52=makeQuery(id+"F5.imprint","IMPRINT",FACE,{"disambiguationData":[TD([[makeQuery(id+"F5.imprint","IMPRINT",EDGE,{"derivedFrom":sQuery(id+"F5.wireOp",EDGE,"E23.9.0.0")}),-1.0]])]});
            var Q53;
            Q53=makeQuery(id+"F5.imprint","IMPRINT",FACE,{"disambiguationData":[TD([[makeQuery(id+"F5.imprint","IMPRINT",EDGE,{"derivedFrom":sQuery(id+"F5.wireOp",EDGE,"E25.0.0.3")}),-1.0]])]});
            var Q54;
            Q54=makeQuery(id+"F5.imprint","IMPRINT",FACE,{"disambiguationData":[TD([[makeQuery(id+"F5.imprint","IMPRINT",EDGE,{"derivedFrom":sQuery(id+"F5.wireOp",EDGE,"E24.0.5.1")}),-1.0]])]});
            var Q55;
            Q55=makeQuery(id+"F5.imprint","IMPRINT",FACE,{"disambiguationData":[TD([[makeQuery(id+"F5.imprint","IMPRINT",EDGE,{"derivedFrom":sQuery(id+"F5.wireOp",EDGE,"E25.18.4.2")}),-1.0]])]});
            var Q56;
            Q56=makeQuery(id+"F5.imprint","IMPRINT",FACE,{"disambiguationData":[TD([[makeQuery(id+"F5.imprint","IMPRINT",EDGE,{"derivedFrom":sQuery(id+"F5.wireOp",EDGE,"E23.8.0.6")}),-1.0]])]});
            var Q57;
            Q57=makeQuery(id+"F5.imprint","IMPRINT",FACE,{"disambiguationData":[TD([[makeQuery(id+"F5.imprint","IMPRINT",EDGE,{"derivedFrom":sQuery(id+"F5.wireOp",EDGE,"E25.18.8.2")}),-1.0]])]});
            var Q58;
            Q58=makeQuery(id+"F5.imprint","IMPRINT",FACE,{"disambiguationData":[TD([[makeQuery(id+"F5.imprint","IMPRINT",EDGE,{"derivedFrom":sQuery(id+"F5.wireOp",EDGE,"E25.18.0.2")}),-1.0]])]});
            var Q59;
            Q59=makeQuery(id+"F5.imprint","IMPRINT",FACE,{"disambiguationData":[TD([[makeQuery(id+"F5.imprint","IMPRINT",EDGE,{"derivedFrom":sQuery(id+"F5.wireOp",EDGE,"E24.18.4.1")}),-1.0]])]});
            var Q60;
            Q60=makeQuery(id+"F5.imprint","IMPRINT",FACE,{"disambiguationData":[TD([[makeQuery(id+"F5.imprint","IMPRINT",EDGE,{"derivedFrom":sQuery(id+"F5.wireOp",EDGE,"E25.0.4.2")}),-1.0]])]});
            var Q61;
            Q61=makeQuery(id+"F5.imprint","IMPRINT",FACE,{"disambiguationData":[TD([[makeQuery(id+"F5.imprint","IMPRINT",EDGE,{"derivedFrom":sQuery(id+"F5.wireOp",EDGE,"E25.0.8.2")}),-1.0]])]});
            var Q62;
            Q62=makeQuery(id+"F5.imprint","IMPRINT",FACE,{"disambiguationData":[TD([[makeQuery(id+"F5.imprint","IMPRINT",EDGE,{"derivedFrom":sQuery(id+"F5.wireOp",EDGE,"E24.0.4.1")}),-1.0]])]});
            var Q63;
            Q63=makeQuery(id+"F5.imprint","IMPRINT",FACE,{"disambiguationData":[TD([[makeQuery(id+"F5.imprint","IMPRINT",EDGE,{"derivedFrom":sQuery(id+"F5.wireOp",EDGE,"E23.8.0.0")}),-1.0]])]});
            var Q64;
            Q64=makeQuery(id+"F5.imprint","IMPRINT",FACE,{"disambiguationData":[TD([[makeQuery(id+"F5.imprint","IMPRINT",EDGE,{"derivedFrom":sQuery(id+"F5.wireOp",EDGE,"E25.0.0.2")}),-1.0]])]});
            var Q65;
            Q65=makeQuery(id+"F5.imprint","IMPRINT",FACE,{"disambiguationData":[TD([[makeQuery(id+"F5.imprint","IMPRINT",EDGE,{"derivedFrom":sQuery(id+"F5.wireOp",EDGE,"E25.0.3.3")}),-1.0]])]});
            var Q66;
            Q66=makeQuery(id+"F5.imprint","IMPRINT",FACE,{"disambiguationData":[TD([[makeQuery(id+"F5.imprint","IMPRINT",EDGE,{"derivedFrom":sQuery(id+"F5.wireOp",EDGE,"E25.0.7.3")}),-1.0]])]});
            var Q67;
            Q67=makeQuery(id+"F5.imprint","IMPRINT",FACE,{"disambiguationData":[TD([[makeQuery(id+"F5.imprint","IMPRINT",EDGE,{"derivedFrom":sQuery(id+"F5.wireOp",EDGE,"E25.0.11.3")}),-1.0]])]});
            var Q68;
            Q68=makeQuery(id+"F5.imprint","IMPRINT",FACE,{"disambiguationData":[TD([[makeQuery(id+"F5.imprint","IMPRINT",EDGE,{"derivedFrom":sQuery(id+"F5.wireOp",EDGE,"E24.0.3.1")}),-1.0]])]});
            var Q69;
            Q69=makeQuery(id+"F5.imprint","IMPRINT",FACE,{"disambiguationData":[TD([[makeQuery(id+"F5.imprint","IMPRINT",EDGE,{"derivedFrom":sQuery(id+"F5.wireOp",EDGE,"E24.0.11.1")}),-1.0]])]});
            var Q70;
            Q70=makeQuery(id+"F5.imprint","IMPRINT",FACE,{"disambiguationData":[TD([[makeQuery(id+"F5.imprint","IMPRINT",EDGE,{"derivedFrom":sQuery(id+"F5.wireOp",EDGE,"E25.18.11.3")}),-1.0]])]});
            var Q71;
            Q71=makeQuery(id+"F5.imprint","IMPRINT",FACE,{"disambiguationData":[TD([[makeQuery(id+"F5.imprint","IMPRINT",EDGE,{"derivedFrom":sQuery(id+"F5.wireOp",EDGE,"E25.18.7.3")}),-1.0]])]});
            var Q72;
            Q72=makeQuery(id+"F5.imprint","IMPRINT",FACE,{"disambiguationData":[TD([[makeQuery(id+"F5.imprint","IMPRINT",EDGE,{"derivedFrom":sQuery(id+"F5.wireOp",EDGE,"E24.18.3.1")}),-1.0]])]});
            var Q73;
            Q73=makeQuery(id+"F5.imprint","IMPRINT",FACE,{"disambiguationData":[TD([[makeQuery(id+"F5.imprint","IMPRINT",EDGE,{"derivedFrom":sQuery(id+"F5.wireOp",EDGE,"E24.18.11.1")}),-1.0]])]});
            var Q74;
            Q74=makeQuery(id+"F5.imprint","IMPRINT",FACE,{"disambiguationData":[TD([[makeQuery(id+"F5.imprint","IMPRINT",EDGE,{"derivedFrom":sQuery(id+"F5.wireOp",EDGE,"E25.18.3.3")}),-1.0]])]});
            var Q75;
            Q75=makeQuery(id+"F5.imprint","IMPRINT",FACE,{"disambiguationData":[TD([[makeQuery(id+"F5.imprint","IMPRINT",EDGE,{"derivedFrom":sQuery(id+"F5.wireOp",EDGE,"E23.5.0.6")}),-1.0]])]});
            var Q76;
            Q76=makeQuery(id+"F5.imprint","IMPRINT",FACE,{"disambiguationData":[TD([[makeQuery(id+"F5.imprint","IMPRINT",EDGE,{"derivedFrom":sQuery(id+"F5.wireOp",EDGE,"E23.4.0.6")}),-1.0]])]});
            var Q77;
            Q77=makeQuery(id+"F5.imprint","IMPRINT",FACE,{"disambiguationData":[TD([[makeQuery(id+"F5.imprint","IMPRINT",EDGE,{"derivedFrom":sQuery(id+"F5.wireOp",EDGE,"E23.5.0.0")}),-1.0]])]});
            var Q78;
            Q78=makeQuery(id+"F5.imprint","IMPRINT",FACE,{"disambiguationData":[TD([[makeQuery(id+"F5.imprint","IMPRINT",EDGE,{"derivedFrom":sQuery(id+"F5.wireOp",EDGE,"E23.3.0.6")}),-1.0]])]});
            var Q79;
            Q79=makeQuery(id+"F5.imprint","IMPRINT",FACE,{"disambiguationData":[TD([[makeQuery(id+"F5.imprint","IMPRINT",EDGE,{"derivedFrom":sQuery(id+"F5.wireOp",EDGE,"E23.2.0.6")}),-1.0]])]});
            var Q80;
            Q80=makeQuery(id+"F5.imprint","IMPRINT",FACE,{"disambiguationData":[TD([[makeQuery(id+"F5.imprint","IMPRINT",EDGE,{"derivedFrom":sQuery(id+"F5.wireOp",EDGE,"E23.2.0.0")}),-1.0]])]});
            var Q81;
            Q81=makeQuery(id+"F5.imprint","IMPRINT",FACE,{"disambiguationData":[TD([[makeQuery(id+"F5.imprint","IMPRINT",EDGE,{"derivedFrom":sQuery(id+"F5.wireOp",EDGE,"E23.1.0.0")}),-1.0]])]});
            var Q82;
            Q82=makeQuery(id+"F5.imprint","IMPRINT",FACE,{"disambiguationData":[TD([[makeQuery(id+"F5.imprint","IMPRINT",EDGE,{"derivedFrom":sQuery(id+"F5.wireOp",EDGE,"E22.0")}),-1.0]])]});
            var Q83;
            Q83=makeQuery(id+"F5.imprint","IMPRINT",FACE,{"disambiguationData":[TD([[makeQuery(id+"F5.imprint","IMPRINT",EDGE,{"derivedFrom":sQuery(id+"F5.wireOp",EDGE,"E19.0")}),-1.0]])]});
            var Q84;
            Q84=makeQuery(id+"F5.imprint","IMPRINT",FACE,{"disambiguationData":[TD([[makeQuery(id+"F5.imprint","IMPRINT",EDGE,{"derivedFrom":sQuery(id+"F5.wireOp",EDGE,"E23.7.0.0")}),-1.0]])]});
            var Q85;
            Q85=makeQuery(id+"F5.imprint","IMPRINT",FACE,{"disambiguationData":[TD([[makeQuery(id+"F5.imprint","IMPRINT",EDGE,{"derivedFrom":sQuery(id+"F5.wireOp",EDGE,"E23.1.0.6")}),-1.0]])]});
            var Q86;
            Q86=makeQuery(id+"F5.imprint","IMPRINT",FACE,{"disambiguationData":[TD([[makeQuery(id+"F5.imprint","IMPRINT",EDGE,{"derivedFrom":sQuery(id+"F5.wireOp",EDGE,"E23.7.0.6")}),-1.0]])]});
            var Q87;
            Q87=makeQuery(id+"F5.imprint","IMPRINT",FACE,{"disambiguationData":[TD([[makeQuery(id+"F5.imprint","IMPRINT",EDGE,{"derivedFrom":sQuery(id+"F5.wireOp",EDGE,"E23.6.0.6")}),-1.0]])]});
            var Q88;
            Q88=makeQuery(id+"F5.imprint","IMPRINT",FACE,{"disambiguationData":[TD([[makeQuery(id+"F5.imprint","IMPRINT",EDGE,{"derivedFrom":sQuery(id+"F5.wireOp",EDGE,"E23.3.0.0")}),-1.0]])]});
            var Q89;
            Q89=makeQuery(id+"F5.imprint","IMPRINT",FACE,{"disambiguationData":[TD([[makeQuery(id+"F5.imprint","IMPRINT",EDGE,{"derivedFrom":sQuery(id+"F5.wireOp",EDGE,"E23.4.0.0")}),-1.0]])]});
            var Q90;
            Q90=makeQuery(id+"F5.imprint","IMPRINT",FACE,{"disambiguationData":[TD([[makeQuery(id+"F5.imprint","IMPRINT",EDGE,{"derivedFrom":sQuery(id+"F5.wireOp",EDGE,"E23.6.0.0")}),-1.0]])]});
            var Q91;
            Q91=makeQuery(id+"F5.imprint","IMPRINT",FACE,{"disambiguationData":[TD([[makeQuery(id+"F5.imprint","IMPRINT",EDGE,{"derivedFrom":sQuery(id+"F5.wireOp",EDGE,"E25.18.3.2")}),-1.0]])]});
            var Q92;
            Q92=makeQuery(id+"F5.imprint","IMPRINT",FACE,{"disambiguationData":[TD([[makeQuery(id+"F5.imprint","IMPRINT",EDGE,{"derivedFrom":sQuery(id+"F5.wireOp",EDGE,"E25.18.7.2")}),-1.0]])]});
            var Q93;
            Q93=makeQuery(id+"F5.imprint","IMPRINT",FACE,{"disambiguationData":[TD([[makeQuery(id+"F5.imprint","IMPRINT",EDGE,{"derivedFrom":sQuery(id+"F5.wireOp",EDGE,"E25.18.11.2")}),-1.0]])]});
            var Q94;
            Q94=makeQuery(id+"F5.imprint","IMPRINT",FACE,{"disambiguationData":[TD([[makeQuery(id+"F5.imprint","IMPRINT",EDGE,{"derivedFrom":sQuery(id+"F5.wireOp",EDGE,"E24.18.2.1")}),-1.0]])]});
            var Q95;
            Q95=makeQuery(id+"F5.imprint","IMPRINT",FACE,{"disambiguationData":[TD([[makeQuery(id+"F5.imprint","IMPRINT",EDGE,{"derivedFrom":sQuery(id+"F5.wireOp",EDGE,"E24.18.10.1")}),-1.0]])]});
            extrude(context, id + "F6", {"entities" : qUnion([Q0, Q1, Q2, Q3, Q4, Q5, Q6, Q7, Q8, Q9, Q10, Q11, Q12, Q13, Q14, Q15, Q16, Q17, Q18, Q19, Q20, Q21, Q22, Q23, Q24, Q25, Q26, Q27, Q28, Q29, Q30, Q31, Q32, Q33, Q34, Q35, Q36, Q37, Q38, Q39, Q40, Q41, Q42, Q43, Q44, Q45, Q46, Q47, Q48, Q49, Q50, Q51, Q52, Q53, Q54, Q55, Q56, Q57, Q58, Q59, Q60, Q61, Q62, Q63, Q64, Q65, Q66, Q67, Q68, Q69, Q70, Q71, Q72, Q73, Q74, Q75, Q76, Q77, Q78, Q79, Q80, Q81, Q82, Q83, Q84, Q85, Q86, Q87, Q88, Q89, Q90, Q91, Q92, Q93, Q94, Q95]), "operationType" : NewBodyOperationType.REMOVE, "endBound" : BoundingType.SYMMETRIC, "depth" : 12.6 * mm});
        }
        {
            var Q0;
            Q0 = qSketchRegion(id + "F3", true);
            extrude(context, id + "F7", {"entities" : qUnion([Q0]), "operationType" : NewBodyOperationType.REMOVE, "oppositeDirection" : true, "depth" : 11 * mm});
        }
    });
